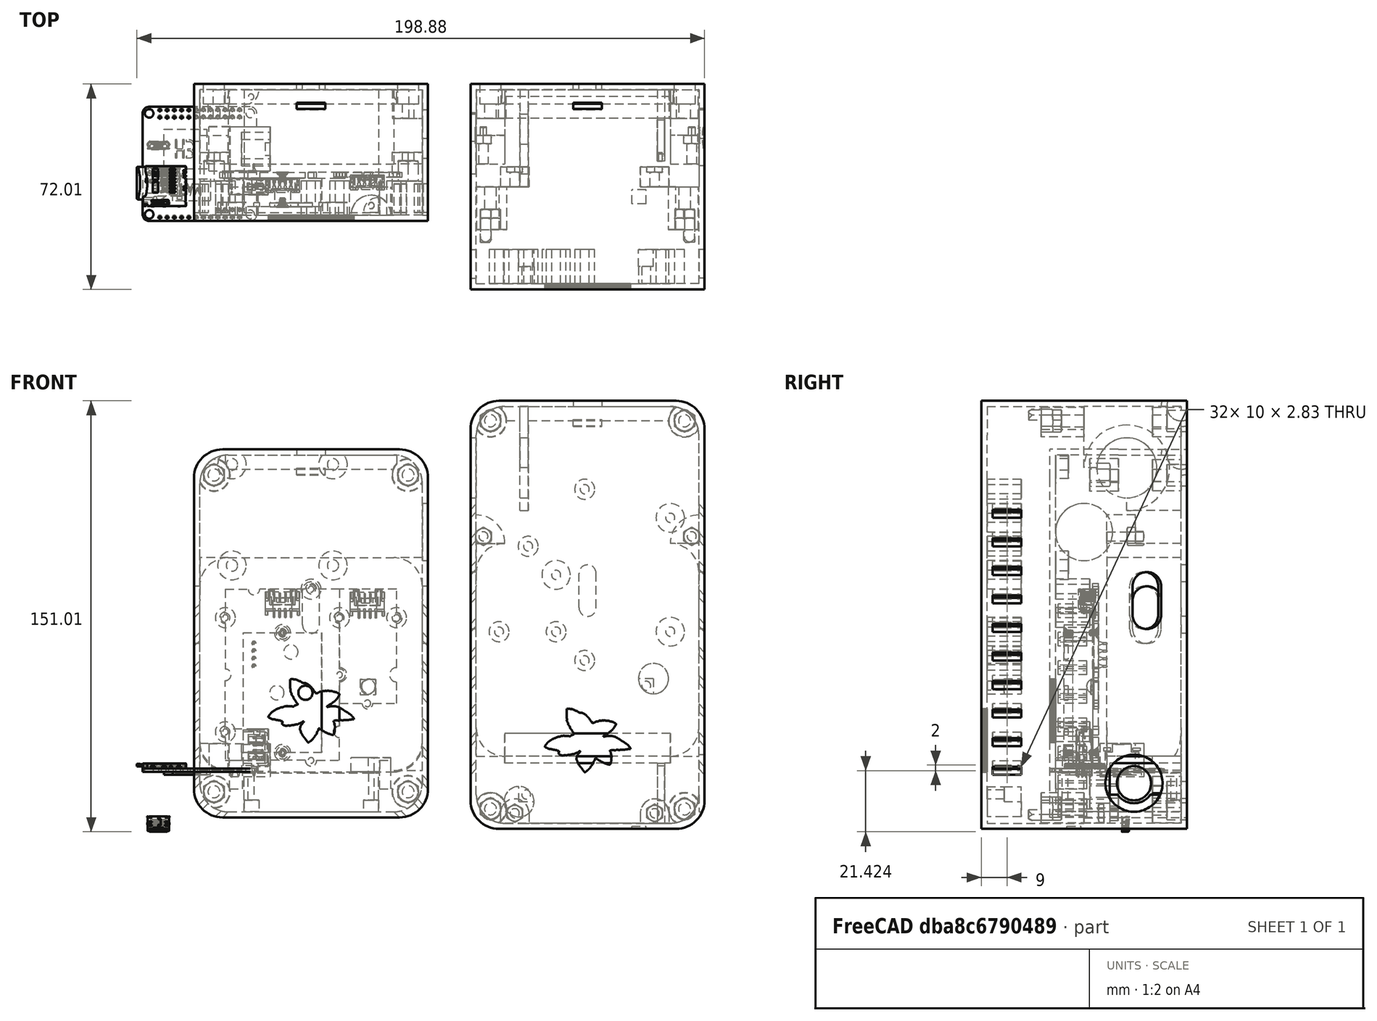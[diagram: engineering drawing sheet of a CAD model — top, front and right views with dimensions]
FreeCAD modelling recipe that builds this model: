
FCSTD DOCUMENT  (FreeCAD 0.20R29410 (Git))
Label: smallerFormFactor
License: All rights reserved
LicenseURL: http://en.wikipedia.org/wiki/All_rights_reserved
objects: Part::Cylinder×180, Part::Cut×129, Part::Box×128, Part::MultiFuse×102, Part::Feature×61, Mesh::Feature×3, App::Part×2, Part::FeaturePython×2
note: 602 computed .brp shape members not serialized (recipe doc carries the construction recipe); baked Part::Feature solids carry a one-line shape summary decoded from their .brp

FEATURE [Part::Feature] Part__Feature  label="NanoPi2_Board"
  shape: bbox 40 x 40 x 1.15 mm, 138 faces (baked)
FEATURE [Part::Feature] Part__Feature001  label="USB_stehend"
  Placement = pos=(16.95,-5.15,8.45) rot=(0.707107,0,0.707107;3.14159rad)
  shape: bbox 13.8 x 6.121 x 16.97 mm, 181 faces (baked)
FEATURE [Part::Feature] Part__Feature002  label="microUSB_Geh㴳e"
  Placement = pos=(-14.4796,6.47188,-20.7085) rot=(0,0,1;0rad)
  shape: bbox 6.984 x 2.203 x 4.218 mm, 441 faces (baked)
FEATURE [Part::Feature] Part__Feature003  label="micro_USB_Innenteil"
  Placement = pos=(-14.4796,6.47188,-16.0085) rot=(0,0,1;0rad)
  shape: bbox 8.008 x 2.958 x 5.47 mm, 792 faces (baked)
FEATURE [App::Part] microUSB
  Group = -> [Part__Feature002,Part__Feature003]
  Origin = -> Origin
  Placement = pos=(-36.1085,-4.22965,-4.14688) rot=(-0.57735,0.57735,0.57735;4.18879rad)
FEATURE [Part::Feature] Part__Feature004  label="microSD Card Connector"
  Placement = pos=(-12.36,-7.8,1.95) rot=(0,0,-1;1.5708rad)
  shape: bbox 15.2 x 14.1 x 1.892 mm, 638 faces (baked)
FEATURE [Part::Feature] Part__Feature005  label="RJ45_tief"
  Placement = pos=(24.7,5.25,4.15) rot=(0,0,1;1.5708rad)
  shape: bbox 21.5 x 15.5 x 11.5 mm, 30 faces (baked)
FEATURE [Part::Feature] Part__Feature006  label="microSD_Card"
  Placement = pos=(-6.76,-12.42,1.9) rot=(1,0,0;1.5708rad)
  shape: bbox 15.24 x 11.43 x 0.889 mm, 332 faces (baked)
FEATURE [Part::Feature] Part__Feature007  label="RAM"
  Placement = pos=(-2.9,-9.1,0) rot=(1,0,0;3.14159rad)
  shape: bbox 13.21 x 7.809 x 1.009 mm, 46 faces (baked)
FEATURE [Part::Feature] Part__Feature008  label="Prozessor_H3"
  Placement = pos=(-5,5.2,1e-15) rot=(1,0,0;3.14159rad)
  shape: bbox 15.01 x 14.01 x 1.009 mm, 28 faces (baked)
FEATURE [Part::Feature] Feature001  label="SCD30"
  Placement = pos=(9,-5,64) rot=(0,1,0;1.5708rad)
  shape: bbox 44 x 15.1 x 64 mm, 422 faces, 13 solids (baked)
FEATURE [Part::Feature] Feature002  label="bme280"
  Placement = pos=(69,-3,63) rot=(0.707107,0,-0.707107;3.14159rad)
  shape: bbox 23.8 x 6.016 x 41.9 mm, 221 faces, 2 solids (baked)
FEATURE [Part::Box] Box001  label="ips7100"
  AttacherType = Attacher::AttachEngine3D
  Height = 43.1
  Length = 47.1
  Width = 13.55
FEATURE [Part::Cylinder] Cylinder
  Angle = 360
  AttacherType = Attacher::AttachEngine3D
  FirstAngle = 0
  Height = 13.55
  Placement = pos=(2.5,13.55,2.5) rot=(1,0,0;1.5708rad)
  Radius = 1
  SecondAngle = 0
FEATURE [Part::Cylinder] Cylinder001  label="semiCut"
  Angle = 90
  AttacherType = Attacher::AttachEngine3D
  FirstAngle = 0
  Height = 4.13
  Placement = pos=(0,4.13,-9e-16) rot=(1,0,0;1.5708rad)
  Radius = 5.25
  SecondAngle = 0
FEATURE [Part::Cylinder] Cylinder002
  Angle = 360
  AttacherType = Attacher::AttachEngine3D
  FirstAngle = 0
  Height = 13.55
  Placement = pos=(2.5,13.55,2.5) rot=(1,0,0;1.5708rad)
  Radius = 1
  SecondAngle = 0
FEATURE [Part::Cylinder] Cylinder003  label="semiCut001"
  Angle = 90
  AttacherType = Attacher::AttachEngine3D
  FirstAngle = 0
  Height = 4.13
  Placement = pos=(0,4.13,-9e-16) rot=(1,0,0;1.5708rad)
  Radius = 5.25
  SecondAngle = 0
FEATURE [Part::MultiFuse] Fusion001  label="ipsCut"
  Shapes = -> [Cylinder,Cylinder001]
FEATURE [Part::MultiFuse] Fusion002  label="ipsCut001"
  Placement = pos=(47.1,0,43.1) rot=(0,1,0;3.14159rad)
  Shapes = -> [Cylinder002,Cylinder003]
FEATURE [Part::MultiFuse] Fusion003
  Shapes = -> [Fusion001,Fusion002]
FEATURE [Part::Cut] Cut  label="ips7100V"
  Base = -> Box001
  Placement = pos=(15.5,26,-14) rot=(1,0,0;1.5708rad)
  Tool = -> Fusion003
FEATURE [Part::Box] Box002  label="V25B"
  AttacherType = Attacher::AttachEngine3D
  Height = 75
  Length = 78
  Width = 26
FEATURE [Part::Box] Box003  label="Cube001"
  AttacherType = Attacher::AttachEngine3D
  Height = 10
  Length = 10
  Width = 26
FEATURE [Part::Box] Box004  label="Cube002"
  AttacherType = Attacher::AttachEngine3D
  Height = 10
  Length = 10
  Width = 26
FEATURE [Part::Box] Box005  label="Cube003"
  AttacherType = Attacher::AttachEngine3D
  Height = 10
  Length = 10
  Width = 26
FEATURE [Part::Box] Box006  label="Cube004"
  AttacherType = Attacher::AttachEngine3D
  Height = 10
  Length = 10
  Width = 26
FEATURE [Part::Cylinder] Cylinder004
  Angle = 90
  AttacherType = Attacher::AttachEngine3D
  FirstAngle = 0
  Height = 26
  Placement = pos=(0,26,-5.8e-15) rot=(1,0,0;1.5708rad)
  Radius = 10
  SecondAngle = 0
FEATURE [Part::Cut] Cut001
  Base = -> Box003
  Placement = pos=(68,0,65) rot=(0,0,1;0rad)
  Tool = -> Cylinder004
FEATURE [Part::Cylinder] Cylinder005
  Angle = 90
  AttacherType = Attacher::AttachEngine3D
  FirstAngle = 0
  Height = 26
  Placement = pos=(0,26,-5.8e-15) rot=(1,0,0;1.5708rad)
  Radius = 10
  SecondAngle = 0
FEATURE [Part::Cut] Cut002
  Base = -> Box004
  Placement = pos=(68,0,10) rot=(0,1,0;1.5708rad)
  Tool = -> Cylinder005
FEATURE [Part::Cylinder] Cylinder006
  Angle = 90
  AttacherType = Attacher::AttachEngine3D
  FirstAngle = 0
  Height = 26
  Placement = pos=(0,26,-5.8e-15) rot=(1,0,0;1.5708rad)
  Radius = 10
  SecondAngle = 0
FEATURE [Part::Cut] Cut003
  Base = -> Box005
  Placement = pos=(10,0,10) rot=(0,1,0;3.14159rad)
  Tool = -> Cylinder006
FEATURE [Part::Cylinder] Cylinder007
  Angle = 90
  AttacherType = Attacher::AttachEngine3D
  FirstAngle = 0
  Height = 26
  Placement = pos=(0,26,-5.8e-15) rot=(1,0,0;1.5708rad)
  Radius = 10
  SecondAngle = 0
FEATURE [Part::Cut] Cut004
  Base = -> Box006
  Placement = pos=(10,0,65) rot=(0,-1,0;1.5708rad)
  Tool = -> Cylinder007
FEATURE [Part::MultiFuse] Fusion004  label="v25Cuts"
  Shapes = -> [Cut001,Cut002,Cut003,Cut004]
FEATURE [Part::Cut] Cut005  label="V25B001"
  Base = -> Box002
  Tool = -> Fusion004
FEATURE [Part::Box] Box009  label="Cube007"
  AttacherType = Attacher::AttachEngine3D
  Height = 10
  Length = 10
  Placement = pos=(0,-10,0) rot=(0,0,1;0rad)
  Width = 36
FEATURE [Part::Box] Box010  label="baseOut001"
  AttacherType = Attacher::AttachEngine3D
  Height = 150
  Length = 82
  Placement = pos=(80,26,-2) rot=(0,0,1;3.14159rad)
  Width = 36
FEATURE [Part::Box] Box011  label="Cube008"
  AttacherType = Attacher::AttachEngine3D
  Height = 10
  Length = 10
  Placement = pos=(0,-10,0) rot=(0,0,1;0rad)
  Width = 36
FEATURE [Part::Box] Box012  label="Cube009"
  AttacherType = Attacher::AttachEngine3D
  Height = 10
  Length = 10
  Placement = pos=(0,-10,0) rot=(0,0,1;0rad)
  Width = 36
FEATURE [Part::Box] Box013  label="Cube010"
  AttacherType = Attacher::AttachEngine3D
  Height = 10
  Length = 10
  Placement = pos=(0,-10,0) rot=(0,0,1;0rad)
  Width = 36
FEATURE [Part::Box] Box014  label="Cube011"
  AttacherType = Attacher::AttachEngine3D
  Height = 10
  Length = 10
  Placement = pos=(0,-8,0) rot=(0,0,1;0rad)
  Width = 34
FEATURE [Part::Box] Box015  label="baseOut002"
  AttacherType = Attacher::AttachEngine3D
  Height = 146
  Length = 78
  Placement = pos=(80,26,-2) rot=(0,0,1;3.14159rad)
  Width = 34
FEATURE [Part::Box] Box016  label="Cube012"
  AttacherType = Attacher::AttachEngine3D
  Height = 10
  Length = 10
  Placement = pos=(0,-8,0) rot=(0,0,1;0rad)
  Width = 34
FEATURE [Part::Box] Box017  label="Cube013"
  AttacherType = Attacher::AttachEngine3D
  Height = 10
  Length = 10
  Placement = pos=(0,-8,0) rot=(0,0,1;0rad)
  Width = 34
FEATURE [Part::Box] Box018  label="Cube014"
  AttacherType = Attacher::AttachEngine3D
  Height = 10
  Length = 10
  Placement = pos=(0,-8,0) rot=(0,0,1;0rad)
  Width = 34
FEATURE [Part::Box] Box019  label="Cube015"
  AttacherType = Attacher::AttachEngine3D
  Height = 10
  Length = 10
  Placement = pos=(10,26,0) rot=(0,0,1;3.14159rad)
  Width = 26
FEATURE [Part::Box] Box020  label="Cube016"
  AttacherType = Attacher::AttachEngine3D
  Height = 10
  Length = 10
  Placement = pos=(10,26,0) rot=(0,0,1;3.14159rad)
  Width = 26
FEATURE [Part::Box] Box021  label="Cube017"
  AttacherType = Attacher::AttachEngine3D
  Height = 10
  Length = 10
  Placement = pos=(10,26,0) rot=(0,0,1;3.14159rad)
  Width = 26
FEATURE [Part::Box] Box022  label="Cube018"
  AttacherType = Attacher::AttachEngine3D
  Height = 10
  Length = 10
  Placement = pos=(10,26,0) rot=(0,0,1;3.14159rad)
  Width = 26
FEATURE [Part::Box] Box023  label="Cube019"
  AttacherType = Attacher::AttachEngine3D
  Height = 4
  Length = 10
  Placement = pos=(8.5,-3,4) rot=(1,0,0;3.14159rad)
  Width = 7
FEATURE [Part::Box] Box024  label="Cube020"
  AttacherType = Attacher::AttachEngine3D
  Height = 4
  Length = 10
  Placement = pos=(57.5,-3,4) rot=(1,0,0;3.14159rad)
  Width = 7
FEATURE [Part::Box] Box025  label="Cube021"
  AttacherType = Attacher::AttachEngine3D
  Height = 22
  Length = 2.5
  Placement = pos=(63.5,24,21) rot=(1,0,0;3.14159rad)
  Width = 25
FEATURE [Part::Box] Box028  label="Cube023"
  AttacherType = Attacher::AttachEngine3D
  Height = 10
  Length = 10
  Placement = pos=(0,-10,0) rot=(0,0,1;0rad)
  Width = 36
FEATURE [Part::Box] Box029  label="baseOut003"
  AttacherType = Attacher::AttachEngine3D
  Height = 150
  Length = 82
  Placement = pos=(80,26,-2) rot=(0,0,1;3.14159rad)
  Width = 36
FEATURE [Part::Box] Box030  label="Cube024"
  AttacherType = Attacher::AttachEngine3D
  Height = 10
  Length = 10
  Placement = pos=(0,-10,0) rot=(0,0,1;0rad)
  Width = 36
FEATURE [Part::Box] Box031  label="Cube025"
  AttacherType = Attacher::AttachEngine3D
  Height = 10
  Length = 10
  Placement = pos=(0,-10,0) rot=(0,0,1;0rad)
  Width = 36
FEATURE [Part::Box] Box032  label="Cube026"
  AttacherType = Attacher::AttachEngine3D
  Height = 10
  Length = 10
  Placement = pos=(0,-10,0) rot=(0,0,1;0rad)
  Width = 36
FEATURE [Part::Box] Box033  label="Cube027"
  AttacherType = Attacher::AttachEngine3D
  Height = 10
  Length = 10
  Placement = pos=(0,-8,0) rot=(0,0,1;0rad)
  Width = 34
FEATURE [Part::Box] Box034  label="baseOut004"
  AttacherType = Attacher::AttachEngine3D
  Height = 146
  Length = 78
  Placement = pos=(80,26,-2) rot=(0,0,1;3.14159rad)
  Width = 34
FEATURE [Part::Box] Box035  label="Cube028"
  AttacherType = Attacher::AttachEngine3D
  Height = 10
  Length = 10
  Placement = pos=(0,-8,0) rot=(0,0,1;0rad)
  Width = 34
FEATURE [Part::Box] Box036  label="Cube029"
  AttacherType = Attacher::AttachEngine3D
  Height = 10
  Length = 10
  Placement = pos=(0,-8,0) rot=(0,0,1;0rad)
  Width = 34
FEATURE [Part::Box] Box037  label="Cube030"
  AttacherType = Attacher::AttachEngine3D
  Height = 10
  Length = 10
  Placement = pos=(0,-8,0) rot=(0,0,1;0rad)
  Width = 34
FEATURE [Part::Box] Box038  label="ethernetHold"
  AttacherType = Attacher::AttachEngine3D
  Height = 34
  Length = 3
  Placement = pos=(15.3,24,109.5) rot=(1,0,0;1.5708rad)
  Width = 37
FEATURE [Part::Box] Box042  label="Cube034"
  AttacherType = Attacher::AttachEngine3D
  Height = 12
  Length = 6
  Placement = pos=(3,0,44) rot=(0,0,1;0rad)
  Width = 2
FEATURE [Part::Box] Box043  label="lightCut"
  AttacherType = Attacher::AttachEngine3D
  Height = 5
  Length = 5
  Placement = pos=(54.5,-16,-6) rot=(0,0,1;0rad)
  Width = 5
FEATURE [Part::Box] Box045  label="Cube036"
  AttacherType = Attacher::AttachEngine3D
  Height = 2
  Length = 20
  Placement = pos=(0,0,0) rot=(0,-1,0;0.785398rad)
  Width = 10
FEATURE [Part::Box] Box046  label="Cube037"
  AttacherType = Attacher::AttachEngine3D
  Height = 2
  Length = 20
  Placement = pos=(0,0,10) rot=(0,-1,0;0.785398rad)
  Width = 10
FEATURE [Part::Box] Box047  label="Cube038"
  AttacherType = Attacher::AttachEngine3D
  Height = 2
  Length = 20
  Placement = pos=(0,0,20) rot=(0,-1,0;0.785398rad)
  Width = 10
FEATURE [Part::Box] Box048  label="Cube039"
  AttacherType = Attacher::AttachEngine3D
  Height = 2
  Length = 20
  Placement = pos=(0,0,30) rot=(0,-1,0;0.785398rad)
  Width = 10
FEATURE [Part::Box] Box049  label="Cube040"
  AttacherType = Attacher::AttachEngine3D
  Height = 2
  Length = 10
  Placement = pos=(0,0,40) rot=(0,-1,0;0.785398rad)
  Width = 10
FEATURE [Part::Box] Box050  label="Cube041"
  AttacherType = Attacher::AttachEngine3D
  Height = 2
  Length = 20
  Placement = pos=(0,0,50) rot=(0,-1,0;0.785398rad)
  Width = 10
FEATURE [Part::Box] Box051  label="Cube042"
  AttacherType = Attacher::AttachEngine3D
  Height = 2
  Length = 20
  Placement = pos=(0,0,60) rot=(0,-1,0;0.785398rad)
  Width = 10
FEATURE [Part::Box] Box052  label="Cube043"
  AttacherType = Attacher::AttachEngine3D
  Height = 2
  Length = 20
  Placement = pos=(0,0,70) rot=(0,-1,0;0.785398rad)
  Width = 10
FEATURE [Part::Box] Box053  label="Cube044"
  AttacherType = Attacher::AttachEngine3D
  Height = 2
  Length = 20
  Placement = pos=(0,0,80) rot=(0,-1,0;0.785398rad)
  Width = 10
FEATURE [Part::Box] Box054  label="Cube045"
  AttacherType = Attacher::AttachEngine3D
  Height = 2
  Length = 20
  Placement = pos=(0,0,90) rot=(0,-1,0;0.785398rad)
  Width = 10
FEATURE [Part::Box] Box055  label="Cube046"
  AttacherType = Attacher::AttachEngine3D
  Height = 2
  Length = 20
  Placement = pos=(0,0,1000) rot=(0,-1,0;0.785398rad)
  Width = 10
FEATURE [Part::Box] Box056  label="Cube047"
  AttacherType = Attacher::AttachEngine3D
  Height = 2
  Length = 20
  Placement = pos=(0,0,0) rot=(0,-1,0;0.785398rad)
  Width = 10
FEATURE [Part::Box] Box057  label="Cube048"
  AttacherType = Attacher::AttachEngine3D
  Height = 2
  Length = 20
  Placement = pos=(0,0,10) rot=(0,-1,0;0.785398rad)
  Width = 10
FEATURE [Part::Box] Box058  label="Cube049"
  AttacherType = Attacher::AttachEngine3D
  Height = 2
  Length = 20
  Placement = pos=(0,0,20) rot=(0,-1,0;0.785398rad)
  Width = 10
FEATURE [Part::Box] Box059  label="Cube050"
  AttacherType = Attacher::AttachEngine3D
  Height = 2
  Length = 20
  Placement = pos=(0,0,30) rot=(0,-1,0;0.785398rad)
  Width = 10
FEATURE [Part::Box] Box060  label="Cube051"
  AttacherType = Attacher::AttachEngine3D
  Height = 2
  Length = 10
  Placement = pos=(0,0,40) rot=(0,-1,0;0.785398rad)
  Width = 10
FEATURE [Part::Box] Box061  label="Cube052"
  AttacherType = Attacher::AttachEngine3D
  Height = 2
  Length = 20
  Placement = pos=(0,0,50) rot=(0,-1,0;0.785398rad)
  Width = 10
FEATURE [Part::Box] Box062  label="Cube053"
  AttacherType = Attacher::AttachEngine3D
  Height = 2
  Length = 20
  Placement = pos=(0,0,60) rot=(0,-1,0;0.785398rad)
  Width = 10
FEATURE [Part::Box] Box063  label="Cube054"
  AttacherType = Attacher::AttachEngine3D
  Height = 2
  Length = 20
  Placement = pos=(0,0,70) rot=(0,-1,0;0.785398rad)
  Width = 10
FEATURE [Part::Box] Box064  label="Cube055"
  AttacherType = Attacher::AttachEngine3D
  Height = 2
  Length = 10
  Placement = pos=(0,0,80) rot=(0,-1,0;0.785398rad)
  Width = 10
FEATURE [Part::Box] Box065  label="Cube056"
  AttacherType = Attacher::AttachEngine3D
  Height = 2
  Length = 20
  Placement = pos=(0,0,90) rot=(0,-1,0;0.785398rad)
  Width = 10
FEATURE [Part::Box] Box066  label="Cube057"
  AttacherType = Attacher::AttachEngine3D
  Height = 2
  Length = 20
  Placement = pos=(0,0,1000) rot=(0,-1,0;0.785398rad)
  Width = 10
FEATURE [Part::Box] Box070  label="Cube059"
  AttacherType = Attacher::AttachEngine3D
  Height = 2.5
  Length = 58
  Placement = pos=(68,24,21) rot=(0,0,1;3.14159rad)
  Width = 10
FEATURE [Part::Box] Box071  label="Cube060"
  AttacherType = Attacher::AttachEngine3D
  Height = 10.5
  Length = 58
  Placement = pos=(68,24,21) rot=(0,0,1;3.14159rad)
  Width = 10
FEATURE [Part::Box] Box072  label="Cube061"
  AttacherType = Attacher::AttachEngine3D
  Height = 1.5
  Length = 36
  Width = 29
FEATURE [Part::Box] Box073  label="Cube062"
  AttacherType = Attacher::AttachEngine3D
  Height = 5.5
  Length = 36
  Placement = pos=(0,0,3.6) rot=(0,0,1;0rad)
  Width = 29
FEATURE [Part::Box] Box074  label="usbCut002"
  AttacherType = Attacher::AttachEngine3D
  Height = 10
  Length = 82
  Width = 20
FEATURE [Part::Box] Box075  label="Cube063"
  AttacherType = Attacher::AttachEngine3D
  Height = 10
  Length = 82
  Width = 5
FEATURE [Part::Box] Box076  label="Cube064"
  AttacherType = Attacher::AttachEngine3D
  Height = 10
  Length = 82
  Width = 5
FEATURE [Part::Box] Box077  label="usbCut004"
  AttacherType = Attacher::AttachEngine3D
  Height = 10
  Length = 82
  Width = 20
FEATURE [Part::Box] Box078  label="Cube065"
  AttacherType = Attacher::AttachEngine3D
  Height = 10
  Length = 82
  Width = 5
FEATURE [Part::Box] Box079  label="Cube066"
  AttacherType = Attacher::AttachEngine3D
  Height = 10
  Length = 82
  Width = 5
FEATURE [Part::Box] Box080  label="ethernetHold001"
  AttacherType = Attacher::AttachEngine3D
  Height = 34
  Length = 3
  Placement = pos=(15.3,5,87.5) rot=(1,0,0;1.5708rad)
  Width = 37
FEATURE [Part::Feature] Clone001  label="m4Nut002"
  Placement = pos=(5,-22.5,141) rot=(-1,0,0;1.5708rad)
  shape: bbox 8.083 x 8.8 x 9.333 mm, 26 faces (baked)
FEATURE [Part::Feature] Clone002  label="m4Nut003"
  Placement = pos=(5,-22.5,141) rot=(-1,0,0;1.5708rad)
  shape: bbox 8.083 x 8.8 x 9.333 mm, 26 faces (baked)
FEATURE [Part::Feature] Clone003  label="m4Nut005"
  Placement = pos=(5,-22.5,141) rot=(-1,0,0;1.5708rad)
  shape: bbox 8.083 x 8.8 x 9.333 mm, 26 faces (baked)
FEATURE [Part::Feature] Clone004  label="m4Nut007"
  Placement = pos=(5,-22.5,141) rot=(-1,0,0;1.5708rad)
  shape: bbox 8.083 x 8.8 x 9.333 mm, 26 faces (baked)
FEATURE [Part::Feature] Clone006  label="m4Nut012"
  Placement = pos=(5,-22.5,141) rot=(-1,0,0;1.5708rad)
  shape: bbox 8.083 x 8.8 x 9.333 mm, 26 faces (baked)
FEATURE [Part::Feature] Clone007  label="m4Nut013"
  Placement = pos=(5,-22.5,141) rot=(-1,0,0;1.5708rad)
  shape: bbox 8.083 x 8.8 x 9.333 mm, 26 faces (baked)
FEATURE [Part::Feature] Clone008  label="m4Nut015"
  Placement = pos=(5,-22.5,141) rot=(-1,0,0;1.5708rad)
  shape: bbox 8.083 x 8.8 x 9.333 mm, 26 faces (baked)
FEATURE [Part::Feature] Clone009  label="m4Nut016"
  Placement = pos=(5,-22.5,141) rot=(-1,0,0;1.5708rad)
  shape: bbox 8.083 x 8.8 x 9.333 mm, 26 faces (baked)
FEATURE [Part::Cylinder] Cylinder008
  Angle = 90
  AttacherType = Attacher::AttachEngine3D
  FirstAngle = 0
  Height = 36
  Placement = pos=(0,26,-5.8e-15) rot=(1,0,0;1.5708rad)
  Radius = 10
  SecondAngle = 0
FEATURE [Part::Cut] Cut006
  Base = -> Box009
  Placement = pos=(8,18,8) rot=(0.707107,0,-0.707107;3.14159rad)
  Tool = -> Cylinder008
FEATURE [Part::Cylinder] Cylinder009
  Angle = 90
  AttacherType = Attacher::AttachEngine3D
  FirstAngle = 0
  Height = 36
  Placement = pos=(0,26,-5.8e-15) rot=(1,0,0;1.5708rad)
  Radius = 10
  SecondAngle = 0
FEATURE [Part::Cut] Cut007
  Base = -> Box011
  Placement = pos=(70,18,8) rot=(1,0,0;3.14159rad)
  Tool = -> Cylinder009
FEATURE [Part::Cylinder] Cylinder010
  Angle = 90
  AttacherType = Attacher::AttachEngine3D
  FirstAngle = 0
  Height = 36
  Placement = pos=(0,26,-5.8e-15) rot=(1,0,0;1.5708rad)
  Radius = 10
  SecondAngle = 0
FEATURE [Part::Cut] Cut008
  Base = -> Box012
  Placement = pos=(8,18,138) rot=(0,0,1;3.14159rad)
  Tool = -> Cylinder010
FEATURE [Part::Cylinder] Cylinder011
  Angle = 90
  AttacherType = Attacher::AttachEngine3D
  FirstAngle = 0
  Height = 36
  Placement = pos=(0,26,-5.8e-15) rot=(1,0,0;1.5708rad)
  Radius = 10
  SecondAngle = 0
FEATURE [Part::Cut] Cut009
  Base = -> Box013
  Placement = pos=(70,18,138) rot=(0.707107,0,0.707107;3.14159rad)
  Tool = -> Cylinder011
FEATURE [Part::Cylinder] Cylinder013
  Angle = 90
  AttacherType = Attacher::AttachEngine3D
  FirstAngle = 0
  Height = 34
  Placement = pos=(0,26,-5.8e-15) rot=(1,0,0;1.5708rad)
  Radius = 10
  SecondAngle = 0
FEATURE [Part::Cut] Cut012
  Base = -> Box014
  Placement = pos=(12,18,8) rot=(0.707107,0,-0.707107;3.14159rad)
  Tool = -> Cylinder013
FEATURE [Part::Cylinder] Cylinder014
  Angle = 90
  AttacherType = Attacher::AttachEngine3D
  FirstAngle = 0
  Height = 34
  Placement = pos=(0,26,-5.8e-15) rot=(1,0,0;1.5708rad)
  Radius = 10
  SecondAngle = 0
FEATURE [Part::Cut] Cut013
  Base = -> Box016
  Placement = pos=(70,18,8) rot=(1,0,0;3.14159rad)
  Tool = -> Cylinder014
FEATURE [Part::Cylinder] Cylinder015
  Angle = 90
  AttacherType = Attacher::AttachEngine3D
  FirstAngle = 0
  Height = 34
  Placement = pos=(0,26,-5.8e-15) rot=(1,0,0;1.5708rad)
  Radius = 10
  SecondAngle = 0
FEATURE [Part::Cut] Cut014
  Base = -> Box017
  Placement = pos=(12,18,134) rot=(0,0,1;3.14159rad)
  Tool = -> Cylinder015
FEATURE [Part::Cylinder] Cylinder016
  Angle = 90
  AttacherType = Attacher::AttachEngine3D
  FirstAngle = 0
  Height = 34
  Placement = pos=(0,26,-5.8e-15) rot=(1,0,0;1.5708rad)
  Radius = 10
  SecondAngle = 0
FEATURE [Part::Cut] Cut015
  Base = -> Box018
  Placement = pos=(70,18,134) rot=(0.707107,0,0.707107;3.14159rad)
  Tool = -> Cylinder016
FEATURE [Part::Cylinder] Cylinder017
  Angle = 90
  AttacherType = Attacher::AttachEngine3D
  FirstAngle = 0
  Height = 26
  Placement = pos=(0,26,-5.8e-15) rot=(1,0,0;1.5708rad)
  Radius = 10
  SecondAngle = 0
FEATURE [Part::Cut] Cut018  label="batterySupport"
  Base = -> Box019
  Placement = pos=(10,-2,33.5) rot=(0,1,0;3.14159rad)
  Tool = -> Cylinder017
FEATURE [Part::Cylinder] Cylinder018
  Angle = 90
  AttacherType = Attacher::AttachEngine3D
  FirstAngle = 0
  Height = 26
  Placement = pos=(0,26,-5.8e-15) rot=(1,0,0;1.5708rad)
  Radius = 10
  SecondAngle = 0
FEATURE [Part::Cut] Cut019  label="batterySupport001"
  Base = -> Box020
  Placement = pos=(68,-2,33.5) rot=(0,1,0;1.5708rad)
  Tool = -> Cylinder018
FEATURE [Part::Cylinder] Cylinder019
  Angle = 90
  AttacherType = Attacher::AttachEngine3D
  FirstAngle = 0
  Height = 26
  Placement = pos=(0,26,-5.8e-15) rot=(1,0,0;1.5708rad)
  Radius = 10
  SecondAngle = 0
FEATURE [Part::Cut] Cut020  label="batterySupport002"
  Base = -> Box021
  Placement = pos=(68,-2,88) rot=(0,0,1;0rad)
  Tool = -> Cylinder019
FEATURE [Part::Cylinder] Cylinder020
  Angle = 90
  AttacherType = Attacher::AttachEngine3D
  FirstAngle = 0
  Height = 26
  Placement = pos=(0,26,-5.8e-15) rot=(1,0,0;1.5708rad)
  Radius = 10
  SecondAngle = 0
FEATURE [Part::Cut] Cut021  label="batterySupport003"
  Base = -> Box022
  Placement = pos=(10,-2,88) rot=(0,-1,0;1.5708rad)
  Tool = -> Cylinder020
FEATURE [Part::Cylinder] Cylinder021
  Angle = 360
  AttacherType = Attacher::AttachEngine3D
  FirstAngle = 0
  Height = 7
  Placement = pos=(13.5,-3,3.5) rot=(1,0,0;1.5708rad)
  Radius = 5
  SecondAngle = 0
FEATURE [Part::Cylinder] Cylinder022
  Angle = 360
  AttacherType = Attacher::AttachEngine3D
  FirstAngle = 0
  Height = 8
  Placement = pos=(13.5,-2,3.5) rot=(1,0,0;1.5708rad)
  Radius = 1.6
  SecondAngle = 0
FEATURE [Part::Cylinder] Cylinder023
  Angle = 360
  AttacherType = Attacher::AttachEngine3D
  FirstAngle = 0
  Height = 7
  Placement = pos=(62.5,-3,3.5) rot=(1,0,0;1.5708rad)
  Radius = 5
  SecondAngle = 0
FEATURE [Part::Cylinder] Cylinder024
  Angle = 360
  AttacherType = Attacher::AttachEngine3D
  FirstAngle = 0
  Height = 8
  Placement = pos=(62.5,-2,3.5) rot=(1,0,0;1.5708rad)
  Radius = 1.6
  SecondAngle = 0
FEATURE [Part::Cylinder] Cylinder025
  Angle = 360
  AttacherType = Attacher::AttachEngine3D
  FirstAngle = 0
  Height = 20
  Radius = 6
  SecondAngle = 0
FEATURE [Part::Cylinder] Cylinder026
  Angle = 360
  AttacherType = Attacher::AttachEngine3D
  FirstAngle = 0
  Height = 5
  Radius = 7
  SecondAngle = 0
FEATURE [Part::Cylinder] Cylinder027  label="mainMounts"
  Angle = 90
  AttacherType = Attacher::AttachEngine3D
  FirstAngle = 0
  Height = 10
  Placement = pos=(0,24,98) rot=(1,0,0;1.5708rad)
  Radius = 10
  SecondAngle = 0
FEATURE [Part::Cylinder] Cylinder028  label="mainMounts001"
  Angle = 90
  AttacherType = Attacher::AttachEngine3D
  FirstAngle = 0
  Height = 10
  Placement = pos=(78,24,98) rot=(0.57735,-0.57735,0.57735;2.0944rad)
  Radius = 10
  SecondAngle = 0
FEATURE [Part::Cylinder] Cylinder029
  Angle = 360
  AttacherType = Attacher::AttachEngine3D
  FirstAngle = 0
  Height = 10
  Placement = pos=(2.5,-2,100.5) rot=(1,0,0;1.5708rad)
  Radius = 1.6
  SecondAngle = 0
FEATURE [Part::Cylinder] Cylinder030
  Angle = 360
  AttacherType = Attacher::AttachEngine3D
  FirstAngle = 0
  Height = 10
  Placement = pos=(75.5,-2,100.5) rot=(1,0,0;1.5708rad)
  Radius = 1.6
  SecondAngle = 0
FEATURE [Part::Cylinder] Cylinder040
  Angle = 90
  AttacherType = Attacher::AttachEngine3D
  FirstAngle = 0
  Height = 36
  Placement = pos=(0,26,-5.8e-15) rot=(1,0,0;1.5708rad)
  Radius = 10
  SecondAngle = 0
FEATURE [Part::Cut] Cut025
  Base = -> Box028
  Placement = pos=(8,18,8) rot=(0.707107,0,-0.707107;3.14159rad)
  Tool = -> Cylinder040
FEATURE [Part::Cylinder] Cylinder041
  Angle = 90
  AttacherType = Attacher::AttachEngine3D
  FirstAngle = 0
  Height = 36
  Placement = pos=(0,26,-5.8e-15) rot=(1,0,0;1.5708rad)
  Radius = 10
  SecondAngle = 0
FEATURE [Part::Cut] Cut026
  Base = -> Box030
  Placement = pos=(70,18,8) rot=(1,0,0;3.14159rad)
  Tool = -> Cylinder041
FEATURE [Part::Cylinder] Cylinder042
  Angle = 90
  AttacherType = Attacher::AttachEngine3D
  FirstAngle = 0
  Height = 36
  Placement = pos=(0,26,-5.8e-15) rot=(1,0,0;1.5708rad)
  Radius = 10
  SecondAngle = 0
FEATURE [Part::Cut] Cut027
  Base = -> Box031
  Placement = pos=(8,18,138) rot=(0,0,1;3.14159rad)
  Tool = -> Cylinder042
FEATURE [Part::Cylinder] Cylinder043
  Angle = 90
  AttacherType = Attacher::AttachEngine3D
  FirstAngle = 0
  Height = 36
  Placement = pos=(0,26,-5.8e-15) rot=(1,0,0;1.5708rad)
  Radius = 10
  SecondAngle = 0
FEATURE [Part::Cut] Cut028
  Base = -> Box032
  Placement = pos=(70,18,138) rot=(0.707107,0,0.707107;3.14159rad)
  Tool = -> Cylinder043
FEATURE [Part::Cylinder] Cylinder044
  Angle = 90
  AttacherType = Attacher::AttachEngine3D
  FirstAngle = 0
  Height = 34
  Placement = pos=(0,26,-5.8e-15) rot=(1,0,0;1.5708rad)
  Radius = 10
  SecondAngle = 0
FEATURE [Part::Cut] Cut030
  Base = -> Box033
  Placement = pos=(12,18,8) rot=(0.707107,0,-0.707107;3.14159rad)
  Tool = -> Cylinder044
FEATURE [Part::Cylinder] Cylinder045
  Angle = 90
  AttacherType = Attacher::AttachEngine3D
  FirstAngle = 0
  Height = 34
  Placement = pos=(0,26,-5.8e-15) rot=(1,0,0;1.5708rad)
  Radius = 10
  SecondAngle = 0
FEATURE [Part::Cut] Cut031
  Base = -> Box035
  Placement = pos=(70,18,8) rot=(1,0,0;3.14159rad)
  Tool = -> Cylinder045
FEATURE [Part::Cylinder] Cylinder046
  Angle = 90
  AttacherType = Attacher::AttachEngine3D
  FirstAngle = 0
  Height = 34
  Placement = pos=(0,26,-5.8e-15) rot=(1,0,0;1.5708rad)
  Radius = 10
  SecondAngle = 0
FEATURE [Part::Cut] Cut032
  Base = -> Box036
  Placement = pos=(12,18,134) rot=(0,0,1;3.14159rad)
  Tool = -> Cylinder046
FEATURE [Part::Cylinder] Cylinder047
  Angle = 90
  AttacherType = Attacher::AttachEngine3D
  FirstAngle = 0
  Height = 34
  Placement = pos=(0,26,-5.8e-15) rot=(1,0,0;1.5708rad)
  Radius = 10
  SecondAngle = 0
FEATURE [Part::Cut] Cut033
  Base = -> Box037
  Placement = pos=(70,18,134) rot=(0.707107,0,0.707107;3.14159rad)
  Tool = -> Cylinder047
FEATURE [Part::Cylinder] Cylinder048
  Angle = 360
  AttacherType = Attacher::AttachEngine3D
  FirstAngle = 0
  Height = 6
  Placement = pos=(17.5,-44,10.05) rot=(-1,0,0;1.5708rad)
  Radius = 1.57
  SecondAngle = 0
FEATURE [Part::Cylinder] Cylinder049
  Angle = 360
  AttacherType = Attacher::AttachEngine3D
  FirstAngle = 0
  Height = 6
  Placement = pos=(15,-44,7.55) rot=(0.57735,0.57735,0.57735;4.18879rad)
  Radius = 5.3
  SecondAngle = 0
FEATURE [Part::Cut] Cut036
  Base = -> Cylinder049
  Tool = -> Cylinder048
FEATURE [Part::Cylinder] Cylinder050
  Angle = 360
  AttacherType = Attacher::AttachEngine3D
  FirstAngle = 0
  Height = 6
  Placement = pos=(62.1,-44,50.65) rot=(0.57735,-0.57735,-0.57735;4.18879rad)
  Radius = 5.3
  SecondAngle = 0
FEATURE [Part::Cylinder] Cylinder051
  Angle = 360
  AttacherType = Attacher::AttachEngine3D
  FirstAngle = 0
  Height = 6
  Placement = pos=(59.6,-44,48.15) rot=(-1,0,0;1.5708rad)
  Radius = 1.57
  SecondAngle = 0
FEATURE [Part::Cut] Cut037
  Base = -> Cylinder050
  Tool = -> Cylinder051
FEATURE [Part::Cylinder] Cylinder052
  Angle = 270
  AttacherType = Attacher::AttachEngine3D
  FirstAngle = 0
  Height = 6
  Placement = pos=(15,-38,7.55) rot=(-1,0,0;1.5708rad)
  Radius = 5.3
  SecondAngle = 0
FEATURE [Part::Cylinder] Cylinder053
  Angle = 270
  AttacherType = Attacher::AttachEngine3D
  FirstAngle = 0
  Height = 6
  Placement = pos=(62.1,-38,50.65) rot=(0,0.707107,0.707107;3.14159rad)
  Radius = 5.3
  SecondAngle = 0
FEATURE [Part::Cylinder] Cylinder054  label="m2HeatSet001"
  Angle = 360
  AttacherType = Attacher::AttachEngine3D
  FirstAngle = 0
  Height = 12
  Placement = pos=(8,-44,67.1) rot=(-1,0,0;1.5708rad)
  Radius = 1.6
  SecondAngle = 0
FEATURE [Part::Cylinder] Cylinder055  label="m2HeatSet002"
  Angle = 360
  AttacherType = Attacher::AttachEngine3D
  FirstAngle = 0
  Height = 12
  Placement = pos=(28,-44,67.1) rot=(-1,0,0;1.5708rad)
  Radius = 1.6
  SecondAngle = 0
FEATURE [Part::Cylinder] Cylinder056  label="m2HeatSet003"
  Angle = 360
  AttacherType = Attacher::AttachEngine3D
  FirstAngle = 0
  Height = 12
  Placement = pos=(68,-44,67.1) rot=(-1,0,0;1.5708rad)
  Radius = 1.6
  SecondAngle = 0
FEATURE [Part::Cylinder] Cylinder057  label="m2HeatSet004"
  Angle = 360
  AttacherType = Attacher::AttachEngine3D
  FirstAngle = 0
  Height = 12
  Placement = pos=(18.2,-44,97) rot=(-1,0,0;1.5708rad)
  Radius = 1.6
  SecondAngle = 0
FEATURE [Part::Cylinder] Cylinder058  label="m2HeatSet005"
  Angle = 360
  AttacherType = Attacher::AttachEngine3D
  FirstAngle = 0
  Height = 12
  Placement = pos=(28,-44,87) rot=(-1,0,0;1.5708rad)
  Radius = 1.6
  SecondAngle = 0
FEATURE [Part::Cylinder] Cylinder059  label="m2HeatSet006"
  Angle = 360
  AttacherType = Attacher::AttachEngine3D
  FirstAngle = 0
  Height = 12
  Placement = pos=(38,-44,117) rot=(-1,0,0;1.5708rad)
  Radius = 1.6
  SecondAngle = 0
FEATURE [Part::Cylinder] Cylinder060  label="m2HeatSet007"
  Angle = 360
  AttacherType = Attacher::AttachEngine3D
  FirstAngle = 0
  Height = 12
  Placement = pos=(38,-44,57) rot=(-1,0,0;1.5708rad)
  Radius = 1.6
  SecondAngle = 0
FEATURE [Part::Cylinder] Cylinder061  label="m2HeatSet008"
  Angle = 360
  AttacherType = Attacher::AttachEngine3D
  FirstAngle = 0
  Height = 12
  Placement = pos=(68,-44,107) rot=(-1,0,0;1.5708rad)
  Radius = 1.6
  SecondAngle = 0
FEATURE [Part::Cylinder] Cylinder062  label="m2HeatSetOut"
  Angle = 360
  AttacherType = Attacher::AttachEngine3D
  FirstAngle = 0
  Height = 12
  Placement = pos=(8,-44,67.1) rot=(-1,0,0;1.5708rad)
  Radius = 3.5
  SecondAngle = 0
FEATURE [Part::Cylinder] Cylinder063  label="m2HeatSetOut001"
  Angle = 360
  AttacherType = Attacher::AttachEngine3D
  FirstAngle = 0
  Height = 12
  Placement = pos=(28,-44,67.1) rot=(-1,0,0;1.5708rad)
  Radius = 3.5
  SecondAngle = 0
FEATURE [Part::Cylinder] Cylinder064  label="m2HeatSetOut002"
  Angle = 360
  AttacherType = Attacher::AttachEngine3D
  FirstAngle = 0
  Height = 12
  Placement = pos=(18.2,-44,97) rot=(-1,0,0;1.5708rad)
  Radius = 3.5
  SecondAngle = 0
FEATURE [Part::Cylinder] Cylinder065  label="m2HeatSetOut003"
  Angle = 360
  AttacherType = Attacher::AttachEngine3D
  FirstAngle = 0
  Height = 12
  Placement = pos=(68,-44,67.1) rot=(-1,0,0;1.5708rad)
  Radius = 5
  SecondAngle = 0
FEATURE [Part::Cylinder] Cylinder066  label="m2HeatSetOut004"
  Angle = 360
  AttacherType = Attacher::AttachEngine3D
  FirstAngle = 0
  Height = 12
  Placement = pos=(28,-44,87) rot=(-1,0,0;1.5708rad)
  Radius = 5
  SecondAngle = 0
FEATURE [Part::Cylinder] Cylinder067  label="m2HeatSetOut005"
  Angle = 360
  AttacherType = Attacher::AttachEngine3D
  FirstAngle = 0
  Height = 12
  Placement = pos=(38,-44,57) rot=(-1,0,0;1.5708rad)
  Radius = 3.5
  SecondAngle = 0
FEATURE [Part::Cylinder] Cylinder068  label="m2HeatSetOut006"
  Angle = 360
  AttacherType = Attacher::AttachEngine3D
  FirstAngle = 0
  Height = 12
  Placement = pos=(68,-44,107) rot=(-1,0,0;1.5708rad)
  Radius = 5
  SecondAngle = 0
FEATURE [Part::Cylinder] Cylinder069  label="m2HeatSetOut007"
  Angle = 360
  AttacherType = Attacher::AttachEngine3D
  FirstAngle = 0
  Height = 12
  Placement = pos=(38,-44,117) rot=(-1,0,0;1.5708rad)
  Radius = 3.5
  SecondAngle = 0
FEATURE [Part::Cylinder] Cylinder073  label="m4SupportDisk"
  Angle = 360
  AttacherType = Attacher::AttachEngine3D
  FirstAngle = 0
  Height = 15
  Placement = pos=(5,-25,141) rot=(-1,0,0;1.5708rad)
  Radius = 5.69
  SecondAngle = 0
FEATURE [Part::Cylinder] Cylinder080  label="m2HeatSetOut008"
  Angle = 360
  AttacherType = Attacher::AttachEngine3D
  FirstAngle = 0
  Height = 12
  Placement = pos=(8,-44,67.1) rot=(-1,0,0;1.5708rad)
  Radius = 3.5
  SecondAngle = 0
FEATURE [Part::Cylinder] Cylinder081  label="m2HeatSet009"
  Angle = 360
  AttacherType = Attacher::AttachEngine3D
  FirstAngle = 0
  Height = 12
  Placement = pos=(8,-44,67.1) rot=(-1,0,0;1.5708rad)
  Radius = 1.6
  SecondAngle = 0
FEATURE [Part::Cut] Cut043  label="m2HeatSet010"
  Base = -> Cylinder080
  Tool = -> Cylinder081
FEATURE [Part::Cylinder] Cylinder084  label="m4HoleBase006"
  Angle = 360
  AttacherType = Attacher::AttachEngine3D
  FirstAngle = 0
  Height = 12
  Placement = pos=(73,26,5) rot=(0,0.707107,-0.707107;3.14159rad)
  Radius = 5.5
  SecondAngle = 0
FEATURE [Part::Cylinder] Cylinder085  label="m4HoleBaseCut"
  Angle = 360
  AttacherType = Attacher::AttachEngine3D
  FirstAngle = 0
  Height = 7
  Placement = pos=(73,26,5) rot=(0,0.707107,-0.707107;3.14159rad)
  Radius = 3.75
  SecondAngle = 0
FEATURE [Part::Cylinder] Cylinder086  label="m4HoleBase007"
  Angle = 360
  AttacherType = Attacher::AttachEngine3D
  FirstAngle = 0
  Height = 12
  Placement = pos=(5,26,5) rot=(0,0.707107,-0.707107;3.14159rad)
  Radius = 5.5
  SecondAngle = 0
FEATURE [Part::Cylinder] Cylinder087  label="m4HoleBaseCut001"
  Angle = 360
  AttacherType = Attacher::AttachEngine3D
  FirstAngle = 0
  Height = 7
  Placement = pos=(5,26,5) rot=(0,0.707107,-0.707107;3.14159rad)
  Radius = 3.75
  SecondAngle = 0
FEATURE [Part::Cylinder] Cylinder088  label="m4HoleBase008"
  Angle = 360
  AttacherType = Attacher::AttachEngine3D
  FirstAngle = 0
  Height = 12
  Placement = pos=(73,26,141) rot=(0,0.707107,-0.707107;3.14159rad)
  Radius = 5.5
  SecondAngle = 0
FEATURE [Part::Cylinder] Cylinder089  label="m4HoleBaseCut002"
  Angle = 360
  AttacherType = Attacher::AttachEngine3D
  FirstAngle = 0
  Height = 7
  Placement = pos=(73,26,141) rot=(0,0.707107,-0.707107;3.14159rad)
  Radius = 3.75
  SecondAngle = 0
FEATURE [Part::Cylinder] Cylinder090  label="m4HoleBase009"
  Angle = 360
  AttacherType = Attacher::AttachEngine3D
  FirstAngle = 0
  Height = 12
  Placement = pos=(5,26,141) rot=(0,0.707107,-0.707107;3.14159rad)
  Radius = 5.5
  SecondAngle = 0
FEATURE [Part::Cylinder] Cylinder091  label="m4HoleBaseCut003"
  Angle = 360
  AttacherType = Attacher::AttachEngine3D
  FirstAngle = 0
  Height = 7
  Placement = pos=(5,26,141) rot=(0,0.707107,-0.707107;3.14159rad)
  Radius = 3.75
  SecondAngle = 0
FEATURE [Part::Cylinder] Cylinder092  label="m4HoleBaseCut004"
  Angle = 360
  AttacherType = Attacher::AttachEngine3D
  FirstAngle = 0
  Height = 7
  Placement = pos=(73,26,5) rot=(0,0.707107,-0.707107;3.14159rad)
  Radius = 2.1
  SecondAngle = 0
FEATURE [Part::Cylinder] Cylinder093  label="m4HoleBaseCut005"
  Angle = 360
  AttacherType = Attacher::AttachEngine3D
  FirstAngle = 0
  Height = 7
  Placement = pos=(5,26,5) rot=(0,0.707107,-0.707107;3.14159rad)
  Radius = 2.1
  SecondAngle = 0
FEATURE [Part::Cylinder] Cylinder094  label="m4HoleBaseCut006"
  Angle = 360
  AttacherType = Attacher::AttachEngine3D
  FirstAngle = 0
  Height = 7
  Placement = pos=(73,26,141) rot=(0,0.707107,-0.707107;3.14159rad)
  Radius = 2.1
  SecondAngle = 0
FEATURE [Part::Cylinder] Cylinder095  label="m4HoleBaseCut007"
  Angle = 360
  AttacherType = Attacher::AttachEngine3D
  FirstAngle = 0
  Height = 7
  Placement = pos=(5,26,141) rot=(0,0.707107,-0.707107;3.14159rad)
  Radius = 2.1
  SecondAngle = 0
FEATURE [Part::Cylinder] Cylinder096
  Angle = 360
  AttacherType = Attacher::AttachEngine3D
  FirstAngle = 0
  Height = 20
  Radius = 6
  SecondAngle = 0
FEATURE [Part::Cylinder] Cylinder097
  Angle = 360
  AttacherType = Attacher::AttachEngine3D
  FirstAngle = 0
  Height = 5
  Radius = 10
  SecondAngle = 0
FEATURE [Part::Cylinder] Cylinder098  label="Ethernet"
  Angle = 360
  AttacherType = Attacher::AttachEngine3D
  FirstAngle = 0
  Height = 36
  Radius = 10.5
  SecondAngle = 0
FEATURE [Part::Cylinder] Cylinder099  label="Ethernet001"
  Angle = 360
  AttacherType = Attacher::AttachEngine3D
  FirstAngle = 0
  Height = 2.25
  Placement = pos=(0,0,13.5) rot=(0,0,1;0rad)
  Radius = 15
  SecondAngle = 0
FEATURE [Part::Cylinder] Cylinder102  label="hookReinforment"
  Angle = 90
  AttacherType = Attacher::AttachEngine3D
  FirstAngle = 0
  Height = 60
  Placement = pos=(9,24,146) rot=(0.57735,-0.57735,0.57735;4.18879rad)
  Radius = 5
  SecondAngle = 0
FEATURE [Part::Cylinder] Cylinder105
  Angle = 360
  AttacherType = Attacher::AttachEngine3D
  FirstAngle = 0
  Height = 2
  Placement = pos=(6,0,44) rot=(0,0.707107,0.707107;3.14159rad)
  Radius = 3
  SecondAngle = 0
FEATURE [Part::Cylinder] Cylinder106
  Angle = 360
  AttacherType = Attacher::AttachEngine3D
  FirstAngle = 0
  Height = 2
  Placement = pos=(6,1.2e-14,56) rot=(0,0.707107,0.707107;3.14159rad)
  Radius = 3
  SecondAngle = 0
FEATURE [Part::Cylinder] Cylinder109
  Angle = 360
  AttacherType = Attacher::AttachEngine3D
  FirstAngle = 0
  Height = 78
  Placement = pos=(-6.8e-15,11.4,30.7) rot=(0,1,0;1.5708rad)
  Radius = 12.5
  SecondAngle = 0
FEATURE [Part::Cut] Cut056
  Base = -> Box071
  Tool = -> Cylinder109
FEATURE [Part::Cylinder] Cylinder110  label="m4SupportDisk001"
  Angle = 360
  AttacherType = Attacher::AttachEngine3D
  FirstAngle = 0
  Height = 15
  Placement = pos=(5,-20.09,141) rot=(-1,0,0;1.5708rad)
  Radius = 5.69
  SecondAngle = 0
FEATURE [Part::Cut] Cut057
  Base = -> Clone001
  Placement = pos=(0,0.5,0) rot=(0,0,1;0rad)
  Tool = -> Cylinder110
FEATURE [Part::Cylinder] Cylinder111  label="m4HoleBaseCut008"
  Angle = 360
  AttacherType = Attacher::AttachEngine3D
  FirstAngle = 0
  Height = 79
  Placement = pos=(5,26,141) rot=(0,0.707107,-0.707107;3.14159rad)
  Radius = 2.1
  SecondAngle = 0
FEATURE [Part::Cylinder] Cylinder112  label="m4SupportDisk002"
  Angle = 360
  AttacherType = Attacher::AttachEngine3D
  FirstAngle = 0
  Height = 15
  Placement = pos=(5,-25,141) rot=(-1,0,0;1.5708rad)
  Radius = 5.69
  SecondAngle = 0
FEATURE [Part::Cylinder] Cylinder113  label="m4SupportDisk003"
  Angle = 360
  AttacherType = Attacher::AttachEngine3D
  FirstAngle = 0
  Height = 15
  Placement = pos=(5,-20.09,141) rot=(-1,0,0;1.5708rad)
  Radius = 5.69
  SecondAngle = 0
FEATURE [Part::Cut] Cut060
  Base = -> Clone002
  Placement = pos=(0,0.5,0) rot=(0,0,1;0rad)
  Tool = -> Cylinder113
FEATURE [Part::Cylinder] Cylinder114  label="m4HoleBaseCut009"
  Angle = 360
  AttacherType = Attacher::AttachEngine3D
  FirstAngle = 0
  Height = 79
  Placement = pos=(5,26,141) rot=(0,0.707107,-0.707107;3.14159rad)
  Radius = 2.1
  SecondAngle = 0
FEATURE [Part::Cylinder] Cylinder115  label="m4SupportDisk004"
  Angle = 360
  AttacherType = Attacher::AttachEngine3D
  FirstAngle = 0
  Height = 15
  Placement = pos=(5,-25,141) rot=(-1,0,0;1.5708rad)
  Radius = 5.69
  SecondAngle = 0
FEATURE [Part::Cylinder] Cylinder116  label="m4SupportDisk005"
  Angle = 360
  AttacherType = Attacher::AttachEngine3D
  FirstAngle = 0
  Height = 15
  Placement = pos=(5,-20.09,141) rot=(-1,0,0;1.5708rad)
  Radius = 5.69
  SecondAngle = 0
FEATURE [Part::Cut] Cut063
  Base = -> Clone003
  Placement = pos=(0,0.5,0) rot=(0,0,1;0rad)
  Tool = -> Cylinder116
FEATURE [Part::Cylinder] Cylinder117  label="m4HoleBaseCut010"
  Angle = 360
  AttacherType = Attacher::AttachEngine3D
  FirstAngle = 0
  Height = 79
  Placement = pos=(5,26,141) rot=(0,0.707107,-0.707107;3.14159rad)
  Radius = 2.1
  SecondAngle = 0
FEATURE [Part::Cylinder] Cylinder118  label="m4SupportDisk006"
  Angle = 360
  AttacherType = Attacher::AttachEngine3D
  FirstAngle = 0
  Height = 15
  Placement = pos=(5,-25,141) rot=(-1,0,0;1.5708rad)
  Radius = 5.69
  SecondAngle = 0
FEATURE [Part::Cylinder] Cylinder119  label="m4SupportDisk007"
  Angle = 360
  AttacherType = Attacher::AttachEngine3D
  FirstAngle = 0
  Height = 15
  Placement = pos=(5,-20.09,141) rot=(-1,0,0;1.5708rad)
  Radius = 5.69
  SecondAngle = 0
FEATURE [Part::Cut] Cut066
  Base = -> Clone004
  Placement = pos=(0,0.5,0) rot=(0,0,1;0rad)
  Tool = -> Cylinder119
FEATURE [Part::Cylinder] Cylinder120  label="m4HoleBaseCut011"
  Angle = 360
  AttacherType = Attacher::AttachEngine3D
  FirstAngle = 0
  Height = 79
  Placement = pos=(5,26,141) rot=(0,0.707107,-0.707107;3.14159rad)
  Radius = 2.1
  SecondAngle = 0
FEATURE [Part::Cylinder] Cylinder122  label="m4SupportDisk009"
  Angle = 360
  AttacherType = Attacher::AttachEngine3D
  FirstAngle = 0
  Height = 15
  Placement = pos=(5,-20.09,141) rot=(-1,0,0;1.5708rad)
  Radius = 5.69
  SecondAngle = 0
FEATURE [Part::Cut] Cut070
  Base = -> Clone006
  Placement = pos=(0,0.5,0) rot=(0,0,1;0rad)
  Tool = -> Cylinder122
FEATURE [Part::Cylinder] Cylinder123  label="m4SupportDisk010"
  Angle = 360
  AttacherType = Attacher::AttachEngine3D
  FirstAngle = 0
  Height = 15
  Placement = pos=(5,-20.09,141) rot=(-1,0,0;1.5708rad)
  Radius = 5.69
  SecondAngle = 0
FEATURE [Part::Cut] Cut071
  Base = -> Clone007
  Placement = pos=(0,0.5,0) rot=(0,0,1;0rad)
  Tool = -> Cylinder123
FEATURE [Part::Cylinder] Cylinder124  label="m4SupportDisk011"
  Angle = 360
  AttacherType = Attacher::AttachEngine3D
  FirstAngle = 0
  Height = 15
  Placement = pos=(5,-20.09,141) rot=(-1,0,0;1.5708rad)
  Radius = 5.69
  SecondAngle = 0
FEATURE [Part::Cut] Cut072
  Base = -> Clone008
  Placement = pos=(0,0.5,0) rot=(0,0,1;0rad)
  Tool = -> Cylinder124
FEATURE [Part::Cylinder] Cylinder125  label="m4SupportDisk012"
  Angle = 360
  AttacherType = Attacher::AttachEngine3D
  FirstAngle = 0
  Height = 15
  Placement = pos=(5,-20.09,141) rot=(-1,0,0;1.5708rad)
  Radius = 5.69
  SecondAngle = 0
FEATURE [Part::Cut] Cut073
  Base = -> Clone009
  Placement = pos=(0,0.5,0) rot=(0,0,1;0rad)
  Tool = -> Cylinder125
FEATURE [Part::Cylinder] Cylinder126
  Angle = 180
  AttacherType = Attacher::AttachEngine3D
  FirstAngle = 0
  Height = 82
  Placement = pos=(0,5,5) rot=(0.707107,0,0.707107;3.14159rad)
  Radius = 5
  SecondAngle = 0
FEATURE [Part::Cut] Cut078  label="cornerCuts002"
  Base = -> Box075
  Tool = -> Cylinder126
FEATURE [Part::Cylinder] Cylinder127
  Angle = 180
  AttacherType = Attacher::AttachEngine3D
  FirstAngle = 0
  Height = 82
  Placement = pos=(0,5,5) rot=(0.707107,0,0.707107;3.14159rad)
  Radius = 5
  SecondAngle = 0
FEATURE [Part::Cut] Cut079  label="cornerCuts003"
  Base = -> Box076
  Placement = pos=(0,20,10) rot=(1,0,0;3.14159rad)
  Tool = -> Cylinder127
FEATURE [Part::Cylinder] Cylinder128
  Angle = 180
  AttacherType = Attacher::AttachEngine3D
  FirstAngle = 0
  Height = 82
  Placement = pos=(0,5,5) rot=(0.707107,0,0.707107;3.14159rad)
  Radius = 5
  SecondAngle = 0
FEATURE [Part::Cut] Cut082  label="cornerCuts004"
  Base = -> Box078
  Tool = -> Cylinder128
FEATURE [Part::Cylinder] Cylinder129
  Angle = 180
  AttacherType = Attacher::AttachEngine3D
  FirstAngle = 0
  Height = 82
  Placement = pos=(0,5,5) rot=(0.707107,0,0.707107;3.14159rad)
  Radius = 5
  SecondAngle = 0
FEATURE [Part::Cut] Cut083  label="cornerCuts005"
  Base = -> Box079
  Placement = pos=(0,20,10) rot=(1,0,0;3.14159rad)
  Tool = -> Cylinder129
FEATURE [Part::Cylinder] Cylinder130
  Angle = 360
  AttacherType = Attacher::AttachEngine3D
  FirstAngle = 0
  Height = 20
  Radius = 6
  SecondAngle = 0
FEATURE [Part::Cylinder] Cylinder131
  Angle = 360
  AttacherType = Attacher::AttachEngine3D
  FirstAngle = 0
  Height = 5
  Radius = 7
  SecondAngle = 0
FEATURE [Part::Cylinder] Cylinder132
  Angle = 360
  AttacherType = Attacher::AttachEngine3D
  FirstAngle = 0
  Height = 8
  Placement = pos=(13.5,-2,3.5) rot=(1,0,0;1.5708rad)
  Radius = 1.6
  SecondAngle = 0
FEATURE [Part::Cylinder] Cylinder133
  Angle = 360
  AttacherType = Attacher::AttachEngine3D
  FirstAngle = 0
  Height = 8
  Placement = pos=(62.5,-2,3.5) rot=(1,0,0;1.5708rad)
  Radius = 1.6
  SecondAngle = 0
FEATURE [Part::Cylinder] Cylinder134
  Angle = 360
  AttacherType = Attacher::AttachEngine3D
  FirstAngle = 0
  Height = 20
  Radius = 6
  SecondAngle = 0
FEATURE [Part::Cylinder] Cylinder135
  Angle = 360
  AttacherType = Attacher::AttachEngine3D
  FirstAngle = 0
  Height = 5
  Radius = 7
  SecondAngle = 0
FEATURE [Part::MultiFuse] Fusion005
  Placement = pos=(0,-2,0) rot=(0,0,1;0rad)
  Shapes = -> [Cut006,Cut007,Cut008,Cut009]
FEATURE [Part::Cut] Cut010  label="BaseOut"
  Base = -> Box010
  Tool = -> Fusion005
FEATURE [Part::MultiFuse] Fusion006
  Shapes = -> [Cut012,Cut013,Cut014,Cut015]
FEATURE [Part::Cut] Cut016  label="BaseOut001"
  Base = -> Box015
  Placement = pos=(-2,-2,2) rot=(0,0,1;0rad)
  Tool = -> Fusion006
FEATURE [Part::Cut] Cut017  label="baseOut"
  Base = -> Cut010
  Tool = -> Cut016
FEATURE [Part::MultiFuse] Fusion007  label="powerSwitch"
  Placement = pos=(71,7.5,14) rot=(0,-1,0;1.5708rad)
  Shapes = -> [Cylinder025,Cylinder026]
FEATURE [Part::MultiFuse] Fusion008  label="base"
  Shapes = -> [Cut017,Cut018,Cut019,Cut020,Cut021]
FEATURE [Part::MultiFuse] Fusion009  label="base001"
  Shapes = -> [Cylinder021,Cylinder023,Box023,Box024,Box025,Fusion008]
FEATURE [Part::MultiFuse] Fusion010  label="baseCuts"
  Shapes = -> [Cylinder024,Cylinder022,Fusion007]
FEATURE [Part::Cut] Cut022  label="base002"
  Base = -> Fusion009
  Tool = -> Fusion010
FEATURE [Part::MultiFuse] Fusion011  label="baseCuts001"
  Placement = pos=(0,10,0) rot=(0,0,1;0rad)
  Shapes = -> [Cylinder029,Cylinder030]
FEATURE [Part::MultiFuse] Fusion012
  Placement = pos=(0,-16,0) rot=(0,0,1;0rad)
  Shapes = -> [Cylinder028,Cylinder027]
FEATURE [Part::MultiFuse] Fusion013  label="base003"
  Shapes = -> [Cut022,Fusion012]
FEATURE [Part::Cut] Cut023  label="baseBottom"
  Base = -> Fusion013
  Tool = -> Fusion011
FEATURE [Part::MultiFuse] Fusion017
  Placement = pos=(0,-2,0) rot=(0,0,1;0rad)
  Shapes = -> [Cut025,Cut026,Cut027,Cut028]
FEATURE [Part::Cut] Cut029  label="BaseOut002"
  Base = -> Box029
  Tool = -> Fusion017
FEATURE [Part::MultiFuse] Fusion018
  Shapes = -> [Cut030,Cut031,Cut032,Cut033]
FEATURE [Part::Cut] Cut034  label="BaseOut003"
  Base = -> Box034
  Placement = pos=(-2,-2,2) rot=(0,0,1;0rad)
  Tool = -> Fusion018
FEATURE [Part::Cut] Cut035  label="baseTop"
  Base = -> Cut029
  Placement = pos=(78,-20,0) rot=(0,0,1;3.14159rad)
  Tool = -> Cut034
FEATURE [Part::MultiFuse] Fusion019  label="baseTop001"
  Shapes = -> [Cut036,Cut037,Cylinder052,Cylinder053,Cut035]
FEATURE [Part::MultiFuse] Fusion020  label="baseTop002"
  Shapes = -> [Cylinder069,Cylinder063,Cylinder064,Cylinder065,Cylinder066,Cylinder067,Cylinder068,Fusion019]
FEATURE [Part::MultiFuse] Fusion021  label="m2HeatSetCuts"
  Shapes = -> [Cylinder062,Cylinder054,Cylinder055,Cylinder056,Cylinder057,Cylinder058,Cylinder059,Cylinder060,Cylinder061]
FEATURE [Part::Cut] Cut038  label="baseTop003"
  Base = -> Fusion020
  Tool = -> Fusion021
FEATURE [Part::MultiFuse] Fusion025  label="baseBottom001"
  Shapes = -> [Cylinder084,Cylinder086,Cylinder088,Cylinder090,Cut023]
FEATURE [Part::MultiFuse] Fusion026  label="m4Cuts"
  Shapes = -> [Cylinder085,Cylinder087,Cylinder089,Cylinder091]
FEATURE [Part::Cut] Cut044  label="baseBottom002"
  Base = -> Fusion025
  Tool = -> Fusion026
FEATURE [Part::MultiFuse] Fusion027  label="m4Cuts001"
  Placement = pos=(0,-5,0) rot=(0,0,1;0rad)
  Shapes = -> [Cylinder092,Cylinder093,Cylinder094,Cylinder095]
FEATURE [Part::Cut] Cut045  label="baseBottom003"
  Base = -> Cut044
  Tool = -> Fusion027
FEATURE [Part::MultiFuse] Fusion028  label="Switch"
  Placement = pos=(83,7.5,14) rot=(0,-1,0;1.5708rad)
  Shapes = -> [Cylinder096,Cylinder097]
FEATURE [Part::MultiFuse] Fusion029  label="EthenetCut"
  Placement = pos=(34,5,124.5) rot=(0,-1,0;1.5708rad)
  Shapes = -> [Cylinder098,Cylinder099]
FEATURE [Part::MultiFuse] Fusion031  label="baseBottom004"
  Shapes = -> [Cut045,Box038]
FEATURE [Part::MultiFuse] Fusion032  label="baseBottom005"
  Shapes = -> [Fusion031,Cylinder102]
FEATURE [Part::MultiFuse] Fusion035  label="voltaicCut"
  Placement = pos=(33,24,31.5) rot=(0,0,1;0rad)
  Shapes = -> [Cylinder106,Cylinder105,Box042]
FEATURE [Part::MultiFuse] Fusion036
  Placement = pos=(-4,-10,15) rot=(0,0,1;0rad)
  Shapes = -> [Box045,Box046,Box047,Box048,Box049,Box050,Box051,Box052,Box053,Box054,Box055]
FEATURE [Part::MultiFuse] Fusion037
  Placement = pos=(82,0,15) rot=(0,0,1;3.14159rad)
  Shapes = -> [Box056,Box057,Box058,Box059,Box060,Box061,Box062,Box063,Box064,Box065,Box066]
FEATURE [Part::MultiFuse] Fusion038  label="vents"
  Placement = pos=(0,-32,0) rot=(0,0,1;0rad)
  Shapes = -> [Fusion036,Fusion037]
FEATURE [Part::MultiFuse] Fusion042  label="baseBottom007"
  Shapes = -> [Cut056,Box070]
FEATURE [Part::MultiFuse] Fusion058  label="topCuts"
  Shapes = -> [Fusion038,Box043]
FEATURE [Part::MultiFuse] Fusion061
  Shapes = -> [Cut078,Cut079]
FEATURE [Part::Cut] Cut080  label="usbCut003"
  Base = -> Box074
  Placement = pos=(-50,16,68) rot=(1,0,0;1.5708rad)
  Tool = -> Fusion061
FEATURE [Part::MultiFuse] Fusion062
  Shapes = -> [Cut082,Cut083]
FEATURE [Part::Cut] Cut084  label="usbCut005"
  Base = -> Box077
  Placement = pos=(50,17,68) rot=(1,0,0;1.5708rad)
  Tool = -> Fusion062
FEATURE [Part::MultiFuse] Fusion063  label="bottomCuts"
  Shapes = -> [Cut080,Cut084,Fusion035]
FEATURE [Part::MultiFuse] Fusion083  label="Switch001"
  Placement = pos=(82,7.5,14) rot=(0,-1,0;1.5708rad)
  Shapes = -> [Cylinder130,Cylinder131]
FEATURE [Part::MultiFuse] Fusion088  label="powerSwitch002"
  Placement = pos=(71,7.5,14) rot=(0,-1,0;1.5708rad)
  Shapes = -> [Cylinder134,Cylinder135]
FEATURE [Part::MultiFuse] Fusion089  label="baseCuts002"
  Shapes = -> [Cylinder133,Cylinder132,Fusion088]
FEATURE [Part::Feature] Part__Feature009  label="m3Nut"
  Placement = pos=(2.5,8,100.5) rot=(1,0,0;1.5708rad)
  shape: bbox 6.352 x 1.801 x 6.352 mm, 26 faces (baked)
FEATURE [Part::Feature] Part__Feature010  label="m3Nut001"
  Placement = pos=(2.5,7,100.5) rot=(1,0,0;1.5708rad)
  shape: bbox 6.352 x 1.801 x 6.352 mm, 26 faces (baked)
FEATURE [Part::Feature] Part__Feature011  label="m3Nut002"
  Placement = pos=(2.5,6,100.5) rot=(1,0,0;1.5708rad)
  shape: bbox 6.352 x 1.801 x 6.352 mm, 26 faces (baked)
FEATURE [Part::MultiFuse] Fusion064  label="m3Cuts"
  Shapes = -> [Part__Feature011,Part__Feature009,Part__Feature010]
FEATURE [Part::Feature] Part__Feature012  label="m3Nut003"
  Placement = pos=(2.5,8,100.5) rot=(1,0,0;1.5708rad)
  shape: bbox 6.352 x 1.801 x 6.352 mm, 26 faces (baked)
FEATURE [Part::Feature] Part__Feature013  label="m3Nut004"
  Placement = pos=(2.5,7,100.5) rot=(1,0,0;1.5708rad)
  shape: bbox 6.352 x 1.801 x 6.352 mm, 26 faces (baked)
FEATURE [Part::Feature] Part__Feature014  label="m3Nut005"
  Placement = pos=(2.5,6,100.5) rot=(1,0,0;1.5708rad)
  shape: bbox 6.352 x 1.801 x 6.352 mm, 26 faces (baked)
FEATURE [Part::MultiFuse] Fusion065  label="m3Cuts001"
  Placement = pos=(73,0,0) rot=(0,0,1;0rad)
  Shapes = -> [Part__Feature014,Part__Feature012,Part__Feature013]
FEATURE [Part::MultiFuse] Fusion066
  Shapes = -> [Fusion065,Fusion064]
FEATURE [Part::Feature] Part__Feature015  label="m3Nut006"
  Placement = pos=(2.5,8,100.5) rot=(1,0,0;1.5708rad)
  shape: bbox 6.352 x 1.801 x 6.352 mm, 26 faces (baked)
FEATURE [Part::Feature] Part__Feature016  label="m3Nut007"
  Placement = pos=(2.5,7,100.5) rot=(1,0,0;1.5708rad)
  shape: bbox 6.352 x 1.801 x 6.352 mm, 26 faces (baked)
FEATURE [Part::Feature] Part__Feature017  label="m3Nut008"
  Placement = pos=(2.5,6,100.5) rot=(1,0,0;1.5708rad)
  shape: bbox 6.352 x 1.801 x 6.352 mm, 26 faces (baked)
FEATURE [Part::MultiFuse] Fusion067  label="m3Cuts002"
  Shapes = -> [Part__Feature017,Part__Feature015,Part__Feature016]
FEATURE [Part::Feature] Part__Feature018  label="m3Nut009"
  Placement = pos=(2.5,8,100.5) rot=(1,0,0;1.5708rad)
  shape: bbox 6.352 x 1.801 x 6.352 mm, 26 faces (baked)
FEATURE [Part::Feature] Part__Feature019  label="m3Nut010"
  Placement = pos=(2.5,7,100.5) rot=(1,0,0;1.5708rad)
  shape: bbox 6.352 x 1.801 x 6.352 mm, 26 faces (baked)
FEATURE [Part::Feature] Part__Feature020  label="m3Nut011"
  Placement = pos=(2.5,6,100.5) rot=(1,0,0;1.5708rad)
  shape: bbox 6.352 x 1.801 x 6.352 mm, 26 faces (baked)
FEATURE [Part::MultiFuse] Fusion068  label="m3Cuts003"
  Placement = pos=(73,0,0) rot=(0,0,1;0rad)
  Shapes = -> [Part__Feature020,Part__Feature018,Part__Feature019]
FEATURE [Part::MultiFuse] Fusion069
  Placement = pos=(0,2,0) rot=(0,0,1;0rad)
  Shapes = -> [Fusion068,Fusion067]
FEATURE [Part::MultiFuse] Fusion070  label="m3Cuts004"
  Shapes = -> [Fusion066,Fusion069]
FEATURE [Part::Feature] Part__Feature021  label="m3Nut012"
  Placement = pos=(2.5,8,100.5) rot=(1,0,0;1.5708rad)
  shape: bbox 6.352 x 1.801 x 6.352 mm, 26 faces (baked)
FEATURE [Part::Feature] Part__Feature022  label="m3Nut013"
  Placement = pos=(2.5,7,100.5) rot=(1,0,0;1.5708rad)
  shape: bbox 6.352 x 1.801 x 6.352 mm, 26 faces (baked)
FEATURE [Part::Feature] Part__Feature023  label="m3Nut014"
  Placement = pos=(2.5,6,100.5) rot=(1,0,0;1.5708rad)
  shape: bbox 6.352 x 1.801 x 6.352 mm, 26 faces (baked)
FEATURE [Part::MultiFuse] Fusion071  label="m3Cuts005"
  Shapes = -> [Part__Feature023,Part__Feature021,Part__Feature022]
FEATURE [Part::Feature] Part__Feature024  label="m3Nut018"
  Placement = pos=(2.5,8,100.5) rot=(1,0,0;1.5708rad)
  shape: bbox 6.352 x 1.801 x 6.352 mm, 26 faces (baked)
FEATURE [Part::Feature] Part__Feature025  label="m3Nut019"
  Placement = pos=(2.5,7,100.5) rot=(1,0,0;1.5708rad)
  shape: bbox 6.352 x 1.801 x 6.352 mm, 26 faces (baked)
FEATURE [Part::Feature] Part__Feature026  label="m3Nut020"
  Placement = pos=(2.5,6,100.5) rot=(1,0,0;1.5708rad)
  shape: bbox 6.352 x 1.801 x 6.352 mm, 26 faces (baked)
FEATURE [Part::MultiFuse] Fusion074  label="m3Cuts007"
  Placement = pos=(0,-3,0) rot=(0,0,1;0rad)
  Shapes = -> [Part__Feature026,Part__Feature024,Part__Feature025]
FEATURE [Part::MultiFuse] Fusion075  label="m3Cuts008"
  Placement = pos=(11,-7,-97) rot=(0,0,1;0rad)
  Shapes = -> [Fusion071,Fusion074]
FEATURE [Part::Feature] Part__Feature027  label="m3Nut021"
  Placement = pos=(2.5,8,100.5) rot=(1,0,0;1.5708rad)
  shape: bbox 6.352 x 1.801 x 6.352 mm, 26 faces (baked)
FEATURE [Part::Feature] Part__Feature028  label="m3Nut022"
  Placement = pos=(2.5,7,100.5) rot=(1,0,0;1.5708rad)
  shape: bbox 6.352 x 1.801 x 6.352 mm, 26 faces (baked)
FEATURE [Part::Feature] Part__Feature029  label="m3Nut023"
  Placement = pos=(2.5,6,100.5) rot=(1,0,0;1.5708rad)
  shape: bbox 6.352 x 1.801 x 6.352 mm, 26 faces (baked)
FEATURE [Part::MultiFuse] Fusion076  label="m3Cuts009"
  Shapes = -> [Part__Feature029,Part__Feature027,Part__Feature028]
FEATURE [Part::Feature] Part__Feature030  label="m3Nut024"
  Placement = pos=(2.5,8,100.5) rot=(1,0,0;1.5708rad)
  shape: bbox 6.352 x 1.801 x 6.352 mm, 26 faces (baked)
FEATURE [Part::Feature] Part__Feature031  label="m3Nut025"
  Placement = pos=(2.5,7,100.5) rot=(1,0,0;1.5708rad)
  shape: bbox 6.352 x 1.801 x 6.352 mm, 26 faces (baked)
FEATURE [Part::Feature] Part__Feature032  label="m3Nut026"
  Placement = pos=(2.5,6,100.5) rot=(1,0,0;1.5708rad)
  shape: bbox 6.352 x 1.801 x 6.352 mm, 26 faces (baked)
FEATURE [Part::MultiFuse] Fusion077  label="m3Cuts010"
  Placement = pos=(0,-3,0) rot=(0,0,1;0rad)
  Shapes = -> [Part__Feature032,Part__Feature030,Part__Feature031]
FEATURE [Part::MultiFuse] Fusion078  label="m3Cuts011"
  Placement = pos=(60,-7,-97) rot=(0,0,1;0rad)
  Shapes = -> [Fusion076,Fusion077]
FEATURE [Part::MultiFuse] Fusion079
  Shapes = -> [Fusion075,Fusion078]
FEATURE [Part::MultiFuse] Fusion080  label="bottomCuts001"
  Shapes = -> [Fusion063,Fusion079]
FEATURE [Part::MultiFuse] Fusion081  label="bottomCuts002"
  Shapes = -> [Fusion070,Fusion080]
FEATURE [Part::MultiFuse] Fusion084  label="bottomCuts003"
  Shapes = -> [Fusion083,Fusion081]
FEATURE [Part::Feature] Solid008  label="m4Nut"
  Placement = pos=(5,-19,141) rot=(-1,0,0;1.5708rad)
  shape: bbox 8.084 x 2.201 x 8.084 mm, 26 faces (baked)
FEATURE [Part::MultiFuse] Fusion044
  Shapes = -> [Cut057,Solid008]
FEATURE [Part::Cut] Cut058  label="m4Hold"
  Base = -> Cylinder073
  Tool = -> Fusion044
FEATURE [Part::Cut] Cut059  label="m4Hold001"
  Base = -> Cut058
  Tool = -> Cylinder111
FEATURE [Part::Feature] Solid009  label="m4Nut004"
  Placement = pos=(5,-19,141) rot=(-1,0,0;1.5708rad)
  shape: bbox 8.084 x 2.201 x 8.084 mm, 26 faces (baked)
FEATURE [Part::MultiFuse] Fusion045
  Shapes = -> [Cut060,Solid009]
FEATURE [Part::Cut] Cut061  label="m4Hold002"
  Base = -> Cylinder112
  Tool = -> Fusion045
FEATURE [Part::Cut] Cut062  label="m4Hold003"
  Base = -> Cut061
  Placement = pos=(68,0,0) rot=(0,0,1;0rad)
  Tool = -> Cylinder114
FEATURE [Part::Feature] Solid010  label="m4Nut006"
  Placement = pos=(5,-19,141) rot=(-1,0,0;1.5708rad)
  shape: bbox 8.084 x 2.201 x 8.084 mm, 26 faces (baked)
FEATURE [Part::MultiFuse] Fusion046
  Shapes = -> [Cut063,Solid010]
FEATURE [Part::Cut] Cut064  label="m4Hold004"
  Base = -> Cylinder115
  Tool = -> Fusion046
FEATURE [Part::Cut] Cut065  label="m4Hold005"
  Base = -> Cut064
  Placement = pos=(68,0,-136) rot=(0,0,1;0rad)
  Tool = -> Cylinder117
FEATURE [Part::Feature] Solid011  label="m4Nut008"
  Placement = pos=(5,-19,141) rot=(-1,0,0;1.5708rad)
  shape: bbox 8.084 x 2.201 x 8.084 mm, 26 faces (baked)
FEATURE [Part::MultiFuse] Fusion047
  Shapes = -> [Cut066,Solid011]
FEATURE [Part::Cut] Cut067  label="m4Hold006"
  Base = -> Cylinder118
  Tool = -> Fusion047
FEATURE [Part::Cut] Cut068  label="m4Hold007"
  Base = -> Cut067
  Placement = pos=(0,0,-136) rot=(0,0,1;0rad)
  Tool = -> Cylinder120
FEATURE [Part::MultiFuse] Fusion048  label="m4Holds"
  Shapes = -> [Cut059,Cut062,Cut065,Cut068]
FEATURE [Part::MultiFuse] Fusion049  label="top"
  Shapes = -> [Cut038,Fusion048]
FEATURE [Part::Feature] Solid013  label="m4Nut011"
  Placement = pos=(5,-19,141) rot=(-1,0,0;1.5708rad)
  shape: bbox 8.084 x 2.201 x 8.084 mm, 26 faces (baked)
FEATURE [Part::MultiFuse] Fusion051
  Shapes = -> [Cut070,Solid013]
FEATURE [Part::Feature] Solid014  label="m4Nut014"
  Placement = pos=(5,-19,141) rot=(-1,0,0;1.5708rad)
  shape: bbox 8.084 x 2.201 x 8.084 mm, 26 faces (baked)
FEATURE [Part::MultiFuse] Fusion052
  Placement = pos=(68,0,0) rot=(0,0,1;0rad)
  Shapes = -> [Cut071,Solid014]
FEATURE [Part::MultiFuse] Fusion053
  Shapes = -> [Fusion051,Fusion052]
FEATURE [Part::Feature] Solid015  label="m4Nut017"
  Placement = pos=(5,-19,141) rot=(-1,0,0;1.5708rad)
  shape: bbox 8.084 x 2.201 x 8.084 mm, 26 faces (baked)
FEATURE [Part::MultiFuse] Fusion054
  Shapes = -> [Cut072,Solid015]
FEATURE [Part::Feature] Solid016  label="m4Nut018"
  Placement = pos=(5,-19,141) rot=(-1,0,0;1.5708rad)
  shape: bbox 8.084 x 2.201 x 8.084 mm, 26 faces (baked)
FEATURE [Part::MultiFuse] Fusion055
  Placement = pos=(68,0,0) rot=(0,0,1;0rad)
  Shapes = -> [Cut073,Solid016]
FEATURE [Part::MultiFuse] Fusion056
  Placement = pos=(0,0,-136) rot=(0,0,1;0rad)
  Shapes = -> [Fusion054,Fusion055]
FEATURE [Part::MultiFuse] Fusion057
  Placement = pos=(0,-3,0) rot=(0,0,1;0rad)
  Shapes = -> [Fusion056,Fusion053]
FEATURE [Part::Cut] Cut074  label="top001"
  Base = -> Fusion049
  Tool = -> Fusion057
FEATURE [Part::Cut] Cut075
  Base = -> Cut074
  Tool = -> Fusion058
FEATURE [Part::MultiFuse] Fusion059  label="top002"
  Shapes = -> [Cut075,Cut043]
FEATURE [Part::FeaturePython] Tube  label="hookCut"  # WARN: FeaturePython — macro-defined, semantics opaque (R4)
  AttacherType = Attacher::AttachEngine3D
  Height = 10
  InnerRadius = 5
  OuterRadius = 7
  Placement = pos=(34,24,146) rot=(0,1,0;1.5708rad)
FEATURE [Part::MultiFuse] Fusion033  label="baseBottomCuts"
  Shapes = -> [Fusion029,Fusion028,Tube]
FEATURE [Part::Cut] Cut046  label="baseBottom006"
  Base = -> Fusion032
  Tool = -> Fusion033
FEATURE [Part::MultiFuse] Fusion082  label="bottom"
  Shapes = -> [Cut046,Fusion042]
FEATURE [Part::Cut] Cut085
  Base = -> Fusion082
  Tool = -> Fusion084
FEATURE [Part::Cut] Cut086  label="bottom001"
  Base = -> Cut085
  Tool = -> Box080
FEATURE [Part::Cut] Cut088  label="bottom002"
  Base = -> Cut086
  Tool = -> Fusion089
FEATURE [Part::Feature] logo3mmWidth001_solid  label="logo3mmWidth001 (Solid)"
  shape: bbox 30 x 22.21 x 4.944 mm, 7244 faces (baked)
FEATURE [Part::MultiFuse] Fusion060
  Shapes = -> [Box072,logo3mmWidth001_solid]
FEATURE [Part::Cut] Cut076  label="logo004"
  Base = -> Fusion060
  Placement = pos=(21,-42.5,14.6) rot=(1,0,0;1.5708rad)
  Tool = -> Box073
FEATURE [Part::Cut] Cut077  label="top003"
  Base = -> Fusion059
  Tool = -> Cut076
FEATURE [Part::MultiFuse] Fusion
  Placement = pos=(96.88,1.99,-18) rot=(0,0,1;0rad)
  Shapes = -> [Cut077,Cut088]
FEATURE [Part::Box] Box081  label="Cube067"
  AttacherType = Attacher::AttachEngine3D
  Height = 10
  Length = 10
  Placement = pos=(0,-10,0) rot=(0,0,1;0rad)
  Width = 36
FEATURE [Part::Box] Box082  label="Cube068"
  AttacherType = Attacher::AttachEngine3D
  Height = 10
  Length = 10
  Placement = pos=(0,-10,0) rot=(0,0,1;0rad)
  Width = 36
FEATURE [Part::Box] Box083  label="Cube069"
  AttacherType = Attacher::AttachEngine3D
  Height = 10
  Length = 10
  Placement = pos=(0,-10,0) rot=(0,0,1;0rad)
  Width = 36
FEATURE [Part::Box] Box084  label="Cube070"
  AttacherType = Attacher::AttachEngine3D
  Height = 10
  Length = 10
  Placement = pos=(0,-10,0) rot=(0,0,1;0rad)
  Width = 36
FEATURE [Part::Cylinder] Cylinder136
  Angle = 90
  AttacherType = Attacher::AttachEngine3D
  FirstAngle = 0
  Height = 36
  Placement = pos=(0,26,-5.8e-15) rot=(1,0,0;1.5708rad)
  Radius = 10
  SecondAngle = 0
FEATURE [Part::Cut] Cut089
  Base = -> Box081
  Placement = pos=(8,6,-6) rot=(0.707107,0,-0.707107;3.14159rad)
  Tool = -> Cylinder136
FEATURE [Part::Cylinder] Cylinder137
  Angle = 90
  AttacherType = Attacher::AttachEngine3D
  FirstAngle = 0
  Height = 36
  Placement = pos=(0,26,-5.8e-15) rot=(1,0,0;1.5708rad)
  Radius = 10
  SecondAngle = 0
FEATURE [Part::Cut] Cut090
  Base = -> Box082
  Placement = pos=(70,6,-6) rot=(1,0,0;3.14159rad)
  Tool = -> Cylinder137
FEATURE [Part::Cylinder] Cylinder138
  Angle = 90
  AttacherType = Attacher::AttachEngine3D
  FirstAngle = 0
  Height = 36
  Placement = pos=(0,26,-5.8e-15) rot=(1,0,0;1.5708rad)
  Radius = 10
  SecondAngle = 0
FEATURE [Part::Cut] Cut091
  Base = -> Box083
  Placement = pos=(8,6,103) rot=(0,0,1;3.14159rad)
  Tool = -> Cylinder138
FEATURE [Part::Cylinder] Cylinder139
  Angle = 90
  AttacherType = Attacher::AttachEngine3D
  FirstAngle = 0
  Height = 36
  Placement = pos=(0,26,-5.8e-15) rot=(1,0,0;1.5708rad)
  Radius = 10
  SecondAngle = 0
FEATURE [Part::Cut] Cut092
  Base = -> Box084
  Placement = pos=(70,6,103) rot=(0.707107,0,0.707107;3.14159rad)
  Tool = -> Cylinder139
FEATURE [Part::Box] Box  label="outerLayer"
  AttacherType = Attacher::AttachEngine3D
  Height = 129
  Length = 82
  Placement = pos=(-2,-20,-16) rot=(0,0,1;0rad)
  Width = 24
FEATURE [Part::Box] Box085  label="Cube"
  AttacherType = Attacher::AttachEngine3D
  Height = 10
  Length = 10
  Width = 10
FEATURE [App::Part] NanoPi2_Board_komplett
  Group = -> [Part__Feature,Part__Feature001,microUSB,Part__Feature004,Part__Feature005,Part__Feature006,Part__Feature007,Part__Feature008,Box085]
  Origin = -> Origin001
  Placement = pos=(29,-13.5,90) rot=(1,0,0;4.71239rad)
FEATURE [Part::Box] Box086  label="innerLayer001"
  AttacherType = Attacher::AttachEngine3D
  Height = 125
  Length = 78
  Placement = pos=(0,-18,-14) rot=(0,0,1;0rad)
  Width = 22
FEATURE [Part::Box] Box087  label="Cube071"
  AttacherType = Attacher::AttachEngine3D
  Height = 10
  Length = 10
  Placement = pos=(0,-10,0) rot=(0,0,1;0rad)
  Width = 36
FEATURE [Part::Box] Box088  label="Cube072"
  AttacherType = Attacher::AttachEngine3D
  Height = 10
  Length = 10
  Placement = pos=(0,-10,0) rot=(0,0,1;0rad)
  Width = 36
FEATURE [Part::Box] Box089  label="Cube073"
  AttacherType = Attacher::AttachEngine3D
  Height = 10
  Length = 10
  Placement = pos=(0,-10,0) rot=(0,0,1;0rad)
  Width = 36
FEATURE [Part::Box] Box090  label="Cube074"
  AttacherType = Attacher::AttachEngine3D
  Height = 10
  Length = 10
  Placement = pos=(0,-10,0) rot=(0,0,1;0rad)
  Width = 36
FEATURE [Part::Cylinder] Cylinder140
  Angle = 90
  AttacherType = Attacher::AttachEngine3D
  FirstAngle = 0
  Height = 36
  Placement = pos=(0,26,-5.8e-15) rot=(1,0,0;1.5708rad)
  Radius = 10
  SecondAngle = 0
FEATURE [Part::Cut] Cut093
  Base = -> Box087
  Placement = pos=(10,6,-4) rot=(0.707107,0,-0.707107;3.14159rad)
  Tool = -> Cylinder140
FEATURE [Part::Cylinder] Cylinder141
  Angle = 90
  AttacherType = Attacher::AttachEngine3D
  FirstAngle = 0
  Height = 36
  Placement = pos=(0,26,-5.8e-15) rot=(1,0,0;1.5708rad)
  Radius = 10
  SecondAngle = 0
FEATURE [Part::Cut] Cut094
  Base = -> Box088
  Placement = pos=(68,6,-4) rot=(1,0,0;3.14159rad)
  Tool = -> Cylinder141
FEATURE [Part::Cylinder] Cylinder142
  Angle = 90
  AttacherType = Attacher::AttachEngine3D
  FirstAngle = 0
  Height = 36
  Placement = pos=(0,26,-5.8e-15) rot=(1,0,0;1.5708rad)
  Radius = 10
  SecondAngle = 0
FEATURE [Part::Cut] Cut095
  Base = -> Box089
  Placement = pos=(10,6,101) rot=(0,0,1;3.14159rad)
  Tool = -> Cylinder142
FEATURE [Part::Cylinder] Cylinder143
  Angle = 90
  AttacherType = Attacher::AttachEngine3D
  FirstAngle = 0
  Height = 36
  Placement = pos=(0,26,-5.8e-15) rot=(1,0,0;1.5708rad)
  Radius = 10
  SecondAngle = 0
FEATURE [Part::Cut] Cut096
  Base = -> Box090
  Placement = pos=(68,6,101) rot=(0.707107,0,0.707107;3.14159rad)
  Tool = -> Cylinder143
FEATURE [Part::MultiFuse] Fusion090  label="outerCuts"
  Shapes = -> [Cut089,Cut090,Cut091,Cut092]
FEATURE [Part::MultiFuse] Fusion091  label="innerCuts"
  Shapes = -> [Cut093,Cut094,Cut095,Cut096]
FEATURE [Part::Cut] Cut097  label="inner"
  Base = -> Box086
  Tool = -> Fusion091
FEATURE [Part::Cut] Cut098  label="outer"
  Base = -> Box
  Tool = -> Fusion090
FEATURE [Part::Cut] Cut099  label="top004"
  Base = -> Cut098
  Tool = -> Cut097
FEATURE [Part::Cylinder] Cylinder144  label="ipsHold"
  Angle = 180
  AttacherType = Attacher::AttachEngine3D
  FirstAngle = 0
  Height = 5
  Placement = pos=(60,-18,0) rot=(0,0,1;0rad)
  Radius = 7
  SecondAngle = 0
FEATURE [Part::Cylinder] Cylinder145  label="ipsHoldCut"
  Angle = 360
  AttacherType = Attacher::AttachEngine3D
  FirstAngle = 0
  Height = 5
  Placement = pos=(60.1,-14.6,0) rot=(0,0,1;0rad)
  Radius = 1.1
  SecondAngle = 0
FEATURE [Part::Cut] Cut100  label="topIn"
  Base = -> Cylinder144
  Tool = -> Cylinder145
FEATURE [Part::Cylinder] Cylinder146  label="m2HeatSetOut009"
  Angle = 360
  AttacherType = Attacher::AttachEngine3D
  FirstAngle = 0
  Height = 12
  Placement = pos=(8,-44,67.1) rot=(-1,0,0;1.5708rad)
  Radius = 3.5
  SecondAngle = 0
FEATURE [Part::Cylinder] Cylinder147  label="m2HeatSet012"
  Angle = 360
  AttacherType = Attacher::AttachEngine3D
  FirstAngle = 0
  Height = 12
  Placement = pos=(8,-44,67.1) rot=(-1,0,0;1.5708rad)
  Radius = 1.6
  SecondAngle = 0
FEATURE [Part::Cut] Cut101  label="m2HeatSet011"
  Base = -> Cylinder146
  Placement = pos=(1,0,-13.1) rot=(0,0,1;0rad)
  Tool = -> Cylinder147
FEATURE [Part::Cylinder] Cylinder148  label="m2HeatSetOut010"
  Angle = 360
  AttacherType = Attacher::AttachEngine3D
  FirstAngle = 0
  Height = 12
  Placement = pos=(8,-44,67.1) rot=(-1,0,0;1.5708rad)
  Radius = 3.5
  SecondAngle = 0
FEATURE [Part::Cylinder] Cylinder149  label="m2HeatSet014"
  Angle = 360
  AttacherType = Attacher::AttachEngine3D
  FirstAngle = 0
  Height = 12
  Placement = pos=(8,-44,67.1) rot=(-1,0,0;1.5708rad)
  Radius = 1.6
  SecondAngle = 0
FEATURE [Part::Cut] Cut102  label="m2HeatSet013"
  Base = -> Cylinder148
  Placement = pos=(1,0,-53.1) rot=(0,0,1;0rad)
  Tool = -> Cylinder149
FEATURE [Part::Cylinder] Cylinder152  label="m2HeatSetOut012"
  Angle = 360
  AttacherType = Attacher::AttachEngine3D
  FirstAngle = 0
  Height = 12
  Placement = pos=(8,-44,67.1) rot=(-1,0,0;1.5708rad)
  Radius = 3.5
  SecondAngle = 0
FEATURE [Part::Cylinder] Cylinder153  label="m2HeatSet018"
  Angle = 360
  AttacherType = Attacher::AttachEngine3D
  FirstAngle = 0
  Height = 12
  Placement = pos=(8,-44,67.1) rot=(-1,0,0;1.5708rad)
  Radius = 1.6
  SecondAngle = 0
FEATURE [Part::Cut] Cut104  label="m2HeatSet017"
  Base = -> Cylinder152
  Placement = pos=(31,0,-3.1) rot=(0,0,1;0rad)
  Tool = -> Cylinder153
FEATURE [Part::Cylinder] Cylinder154  label="m2HeatSetOut013"
  Angle = 360
  AttacherType = Attacher::AttachEngine3D
  FirstAngle = 0
  Height = 12
  Placement = pos=(8,-44,67.1) rot=(-1,0,0;1.5708rad)
  Radius = 3.5
  SecondAngle = 0
FEATURE [Part::Cylinder] Cylinder155  label="m2HeatSet020"
  Angle = 360
  AttacherType = Attacher::AttachEngine3D
  FirstAngle = 0
  Height = 12
  Placement = pos=(8,-44,67.1) rot=(-1,0,0;1.5708rad)
  Radius = 1.6
  SecondAngle = 0
FEATURE [Part::Cut] Cut105  label="m2HeatSet019"
  Base = -> Cylinder154
  Placement = pos=(41,0,-13.1) rot=(0,0,1;0rad)
  Tool = -> Cylinder155
FEATURE [Part::Cylinder] Cylinder160  label="m2HeatSetOut016"
  Angle = 360
  AttacherType = Attacher::AttachEngine3D
  FirstAngle = 0
  Height = 12
  Placement = pos=(8,-44,67.1) rot=(-1,0,0;1.5708rad)
  Radius = 3.5
  SecondAngle = 0
FEATURE [Part::Cylinder] Cylinder161  label="m2HeatSet026"
  Angle = 360
  AttacherType = Attacher::AttachEngine3D
  FirstAngle = 0
  Height = 12
  Placement = pos=(8,-44,67.1) rot=(-1,0,0;1.5708rad)
  Radius = 1.6
  SecondAngle = 0
FEATURE [Part::Cut] Cut108  label="m2HeatSet025"
  Base = -> Cylinder160
  Placement = pos=(61,0,-13.1) rot=(0,0,1;0rad)
  Tool = -> Cylinder161
FEATURE [Part::Cylinder] Cylinder162  label="m2HeatSetOut017"
  Angle = 360
  AttacherType = Attacher::AttachEngine3D
  FirstAngle = 0
  Height = 4.5
  Placement = pos=(8,-44,67.1) rot=(-1,0,0;1.5708rad)
  Radius = 5
  SecondAngle = 0
FEATURE [Part::Cylinder] Cylinder163  label="m2HeatSet028"
  Angle = 360
  AttacherType = Attacher::AttachEngine3D
  FirstAngle = 0
  Height = 12
  Placement = pos=(8,-44,67.1) rot=(-1,0,0;1.5708rad)
  Radius = 2
  SecondAngle = 0
FEATURE [Part::Cut] Cut109  label="m3HeatSet027"
  Base = -> Cylinder162
  Placement = pos=(3.3,0,5.2) rot=(0,0,1;0rad)
  Tool = -> Cylinder163
FEATURE [Part::Cylinder] Cylinder164  label="m2HeatSetOut018"
  Angle = 360
  AttacherType = Attacher::AttachEngine3D
  FirstAngle = 0
  Height = 4.5
  Placement = pos=(8,-44,67.1) rot=(-1,0,0;1.5708rad)
  Radius = 5
  SecondAngle = 0
FEATURE [Part::Cylinder] Cylinder165  label="m2HeatSet029"
  Angle = 360
  AttacherType = Attacher::AttachEngine3D
  FirstAngle = 0
  Height = 12
  Placement = pos=(8,-44,67.1) rot=(-1,0,0;1.5708rad)
  Radius = 2
  SecondAngle = 0
FEATURE [Part::Cut] Cut110  label="m3HeatSet028"
  Base = -> Cylinder164
  Placement = pos=(38.7,0,5.2) rot=(0,0,1;0rad)
  Tool = -> Cylinder165
FEATURE [Part::Cylinder] Cylinder166  label="m2HeatSetOut019"
  Angle = 360
  AttacherType = Attacher::AttachEngine3D
  FirstAngle = 0
  Height = 4.5
  Placement = pos=(8,-44,67.1) rot=(-1,0,0;1.5708rad)
  Radius = 5
  SecondAngle = 0
FEATURE [Part::Cylinder] Cylinder167  label="m2HeatSet030"
  Angle = 360
  AttacherType = Attacher::AttachEngine3D
  FirstAngle = 0
  Height = 12
  Placement = pos=(8,-44,67.1) rot=(-1,0,0;1.5708rad)
  Radius = 2
  SecondAngle = 0
FEATURE [Part::Cut] Cut111  label="m3HeatSet029"
  Base = -> Cylinder166
  Placement = pos=(3.3,0,40.6) rot=(0,0,1;0rad)
  Tool = -> Cylinder167
FEATURE [Part::Cylinder] Cylinder168  label="m2HeatSetOut020"
  Angle = 360
  AttacherType = Attacher::AttachEngine3D
  FirstAngle = 0
  Height = 4.5
  Placement = pos=(8,-44,67.1) rot=(-1,0,0;1.5708rad)
  Radius = 5
  SecondAngle = 0
FEATURE [Part::Cylinder] Cylinder169  label="m2HeatSet031"
  Angle = 360
  AttacherType = Attacher::AttachEngine3D
  FirstAngle = 0
  Height = 12
  Placement = pos=(8,-44,67.1) rot=(-1,0,0;1.5708rad)
  Radius = 2
  SecondAngle = 0
FEATURE [Part::Cut] Cut112  label="m3HeatSet030"
  Base = -> Cylinder168
  Placement = pos=(38.7,0,40.6) rot=(0,0,1;0rad)
  Tool = -> Cylinder169
FEATURE [Part::MultiFuse] Fusion092  label="topIn001"
  Placement = pos=(0,26,0) rot=(0,0,1;0rad)
  Shapes = -> [Cut101,Cut102,Cut104,Cut105,Cut108,Cut109,Cut110,Cut111,Cut112]
FEATURE [Part::Feature] Clone010  label="m4Nut019"
  Placement = pos=(5,-22.5,141) rot=(-1,0,0;1.5708rad)
  shape: bbox 8.083 x 8.8 x 9.333 mm, 26 faces (baked)
FEATURE [Part::Cylinder] Cylinder170  label="m4SupportDisk013"
  Angle = 360
  AttacherType = Attacher::AttachEngine3D
  FirstAngle = 0
  Height = 10
  Placement = pos=(5,-25,141) rot=(-1,0,0;1.5708rad)
  Radius = 5.69
  SecondAngle = 0
FEATURE [Part::Cylinder] Cylinder171  label="m4SupportDisk014"
  Angle = 360
  AttacherType = Attacher::AttachEngine3D
  FirstAngle = 0
  Height = 15
  Placement = pos=(5,-20.09,141) rot=(-1,0,0;1.5708rad)
  Radius = 5.69
  SecondAngle = 0
FEATURE [Part::Cut] Cut113
  Base = -> Clone010
  Placement = pos=(0,0.5,0) rot=(0,0,1;0rad)
  Tool = -> Cylinder171
FEATURE [Part::Cylinder] Cylinder172  label="m4HoleBaseCut012"
  Angle = 360
  AttacherType = Attacher::AttachEngine3D
  FirstAngle = 0
  Height = 79
  Placement = pos=(5,26,141) rot=(0,0.707107,-0.707107;3.14159rad)
  Radius = 2.1
  SecondAngle = 0
FEATURE [Part::Feature] Solid017  label="m4Nut020"
  Placement = pos=(5,-19,141) rot=(-1,0,0;1.5708rad)
  shape: bbox 8.084 x 2.201 x 8.084 mm, 26 faces (baked)
FEATURE [Part::MultiFuse] Fusion093
  Shapes = -> [Cut113,Solid017]
FEATURE [Part::Cut] Cut114  label="m4Hold008"
  Base = -> Cylinder170
  Tool = -> Fusion093
FEATURE [Part::Cut] Cut115  label="m4Hold009"
  Base = -> Cut114
  Placement = pos=(0,19,-148) rot=(0,0,1;0rad)
  Tool = -> Cylinder172
FEATURE [Part::Feature] Clone011  label="m4Nut021"
  Placement = pos=(5,-22.5,141) rot=(-1,0,0;1.5708rad)
  shape: bbox 8.083 x 8.8 x 9.333 mm, 26 faces (baked)
FEATURE [Part::Cylinder] Cylinder173  label="m4SupportDisk015"
  Angle = 360
  AttacherType = Attacher::AttachEngine3D
  FirstAngle = 0
  Height = 10
  Placement = pos=(5,-25,141) rot=(-1,0,0;1.5708rad)
  Radius = 5.69
  SecondAngle = 0
FEATURE [Part::Cylinder] Cylinder174  label="m4SupportDisk016"
  Angle = 360
  AttacherType = Attacher::AttachEngine3D
  FirstAngle = 0
  Height = 15
  Placement = pos=(5,-20.09,141) rot=(-1,0,0;1.5708rad)
  Radius = 5.69
  SecondAngle = 0
FEATURE [Part::Cut] Cut116
  Base = -> Clone011
  Placement = pos=(0,0.5,0) rot=(0,0,1;0rad)
  Tool = -> Cylinder174
FEATURE [Part::Cylinder] Cylinder175  label="m4HoleBaseCut013"
  Angle = 360
  AttacherType = Attacher::AttachEngine3D
  FirstAngle = 0
  Height = 79
  Placement = pos=(5,26,141) rot=(0,0.707107,-0.707107;3.14159rad)
  Radius = 2.1
  SecondAngle = 0
FEATURE [Part::Feature] Solid018  label="m4Nut022"
  Placement = pos=(5,-19,141) rot=(-1,0,0;1.5708rad)
  shape: bbox 8.084 x 2.201 x 8.084 mm, 26 faces (baked)
FEATURE [Part::MultiFuse] Fusion094
  Shapes = -> [Cut116,Solid018]
FEATURE [Part::Cut] Cut117  label="m4Hold010"
  Base = -> Cylinder173
  Tool = -> Fusion094
FEATURE [Part::Cut] Cut118  label="m4Hold011"
  Base = -> Cut117
  Placement = pos=(68,19,-148) rot=(0,0,1;0rad)
  Tool = -> Cylinder175
FEATURE [Part::Feature] Clone012  label="m4Nut023"
  Placement = pos=(5,-22.5,141) rot=(-1,0,0;1.5708rad)
  shape: bbox 8.083 x 8.8 x 9.333 mm, 26 faces (baked)
FEATURE [Part::Feature] Clone013  label="m4Nut024"
  Placement = pos=(5,-22.5,141) rot=(-1,0,0;1.5708rad)
  shape: bbox 8.083 x 8.8 x 9.333 mm, 26 faces (baked)
FEATURE [Part::Cylinder] Cylinder176  label="m4SupportDisk017"
  Angle = 360
  AttacherType = Attacher::AttachEngine3D
  FirstAngle = 0
  Height = 10
  Placement = pos=(5,-25,141) rot=(-1,0,0;1.5708rad)
  Radius = 5.69
  SecondAngle = 0
FEATURE [Part::Cylinder] Cylinder177  label="m4SupportDisk018"
  Angle = 360
  AttacherType = Attacher::AttachEngine3D
  FirstAngle = 0
  Height = 15
  Placement = pos=(5,-20.09,141) rot=(-1,0,0;1.5708rad)
  Radius = 5.69
  SecondAngle = 0
FEATURE [Part::Cut] Cut119
  Base = -> Clone012
  Placement = pos=(0,0.5,0) rot=(0,0,1;0rad)
  Tool = -> Cylinder177
FEATURE [Part::Cylinder] Cylinder178  label="m4HoleBaseCut014"
  Angle = 360
  AttacherType = Attacher::AttachEngine3D
  FirstAngle = 0
  Height = 79
  Placement = pos=(5,26,141) rot=(0,0.707107,-0.707107;3.14159rad)
  Radius = 2.1
  SecondAngle = 0
FEATURE [Part::Cylinder] Cylinder179  label="m4SupportDisk019"
  Angle = 360
  AttacherType = Attacher::AttachEngine3D
  FirstAngle = 0
  Height = 10
  Placement = pos=(5,-25,141) rot=(-1,0,0;1.5708rad)
  Radius = 5.69
  SecondAngle = 0
FEATURE [Part::Cylinder] Cylinder180  label="m4SupportDisk020"
  Angle = 360
  AttacherType = Attacher::AttachEngine3D
  FirstAngle = 0
  Height = 15
  Placement = pos=(5,-20.09,141) rot=(-1,0,0;1.5708rad)
  Radius = 5.69
  SecondAngle = 0
FEATURE [Part::Cut] Cut122
  Base = -> Clone013
  Placement = pos=(0,0.5,0) rot=(0,0,1;0rad)
  Tool = -> Cylinder180
FEATURE [Part::Cylinder] Cylinder181  label="m4HoleBaseCut015"
  Angle = 360
  AttacherType = Attacher::AttachEngine3D
  FirstAngle = 0
  Height = 79
  Placement = pos=(5,26,141) rot=(0,0.707107,-0.707107;3.14159rad)
  Radius = 2.1
  SecondAngle = 0
FEATURE [Part::Feature] Solid019  label="m4Nut025"
  Placement = pos=(5,-19,141) rot=(-1,0,0;1.5708rad)
  shape: bbox 8.084 x 2.201 x 8.084 mm, 26 faces (baked)
FEATURE [Part::MultiFuse] Fusion095
  Shapes = -> [Cut119,Solid019]
FEATURE [Part::Cut] Cut120  label="m4Hold012"
  Base = -> Cylinder176
  Tool = -> Fusion095
FEATURE [Part::Cut] Cut121  label="m4Hold013"
  Base = -> Cut120
  Placement = pos=(0,19,-37) rot=(0,0,1;0rad)
  Tool = -> Cylinder178
FEATURE [Part::Feature] Solid020  label="m4Nut026"
  Placement = pos=(5,-19,141) rot=(-1,0,0;1.5708rad)
  shape: bbox 8.084 x 2.201 x 8.084 mm, 26 faces (baked)
FEATURE [Part::MultiFuse] Fusion096
  Shapes = -> [Cut122,Solid020]
FEATURE [Part::Cut] Cut123  label="m4Hold014"
  Base = -> Cylinder179
  Tool = -> Fusion096
FEATURE [Part::Cut] Cut124  label="m4Hold015"
  Base = -> Cut123
  Placement = pos=(68,19,-37) rot=(0,0,1;0rad)
  Tool = -> Cylinder181
FEATURE [Part::Cylinder] Cylinder182 .. Cylinder189  x8 (patterned run collapsed; names and placements below)
  Angle = 90
  AttacherType = Attacher::AttachEngine3D
  FirstAngle = 0
  Height = 36
  Radius = 10
  SecondAngle = 0
  placements: all 8 at pos=(0,26,-5.8e-15) rot=(1,0,0;1.5708rad)
FEATURE [Part::Box] Box092  label="Cube075"
  AttacherType = Attacher::AttachEngine3D
  Height = 10
  Length = 10
  Placement = pos=(0,-10,0) rot=(0,0,1;0rad)
  Width = 36
FEATURE [Part::Box] Box093  label="Cube076"
  AttacherType = Attacher::AttachEngine3D
  Height = 10
  Length = 10
  Placement = pos=(0,-10,0) rot=(0,0,1;0rad)
  Width = 36
FEATURE [Part::Box] Box094  label="Cube077"
  AttacherType = Attacher::AttachEngine3D
  Height = 10
  Length = 10
  Placement = pos=(0,-10,0) rot=(0,0,1;0rad)
  Width = 36
FEATURE [Part::Box] Box095  label="Cube078"
  AttacherType = Attacher::AttachEngine3D
  Height = 10
  Length = 10
  Placement = pos=(0,-10,0) rot=(0,0,1;0rad)
  Width = 36
FEATURE [Part::Box] Box097  label="Cube079"
  AttacherType = Attacher::AttachEngine3D
  Height = 10
  Length = 10
  Placement = pos=(0,-10,0) rot=(0,0,1;0rad)
  Width = 36
FEATURE [Part::Box] Box098  label="Cube080"
  AttacherType = Attacher::AttachEngine3D
  Height = 10
  Length = 10
  Placement = pos=(0,-10,0) rot=(0,0,1;0rad)
  Width = 36
FEATURE [Part::Box] Box099  label="Cube081"
  AttacherType = Attacher::AttachEngine3D
  Height = 10
  Length = 10
  Placement = pos=(0,-10,0) rot=(0,0,1;0rad)
  Width = 36
FEATURE [Part::Box] Box100  label="Cube082"
  AttacherType = Attacher::AttachEngine3D
  Height = 10
  Length = 10
  Placement = pos=(0,-10,0) rot=(0,0,1;0rad)
  Width = 36
FEATURE [Part::Cut] Cut125
  Base = -> Box092
  Placement = pos=(8,6,-6) rot=(0.707107,0,-0.707107;3.14159rad)
  Tool = -> Cylinder182
FEATURE [Part::Cut] Cut126
  Base = -> Box093
  Placement = pos=(70,6,-6) rot=(1,0,0;3.14159rad)
  Tool = -> Cylinder183
FEATURE [Part::Cut] Cut127
  Base = -> Box094
  Placement = pos=(8,6,103) rot=(0,0,1;3.14159rad)
  Tool = -> Cylinder184
FEATURE [Part::Cut] Cut128
  Base = -> Box095
  Placement = pos=(70,6,103) rot=(0.707107,0,0.707107;3.14159rad)
  Tool = -> Cylinder185
FEATURE [Part::Cut] Cut129
  Base = -> Box097
  Placement = pos=(10,6,-4) rot=(0.707107,0,-0.707107;3.14159rad)
  Tool = -> Cylinder186
FEATURE [Part::Cut] Cut130
  Base = -> Box098
  Placement = pos=(68,6,-4) rot=(1,0,0;3.14159rad)
  Tool = -> Cylinder187
FEATURE [Part::Cut] Cut131
  Base = -> Box099
  Placement = pos=(10,6,101) rot=(0,0,1;3.14159rad)
  Tool = -> Cylinder188
FEATURE [Part::Cut] Cut132
  Base = -> Box100
  Placement = pos=(68,6,101) rot=(0.707107,0,0.707107;3.14159rad)
  Tool = -> Cylinder189
FEATURE [Part::MultiFuse] Fusion097  label="outerCuts001"
  Shapes = -> [Cut125,Cut126,Cut127,Cut128]
FEATURE [Part::MultiFuse] Fusion098  label="innerCuts001"
  Shapes = -> [Cut129,Cut130,Cut131,Cut132]
FEATURE [Part::Box] Box091  label="outerLayer001"
  AttacherType = Attacher::AttachEngine3D
  Height = 129
  Length = 82
  Placement = pos=(-2,-20,-16) rot=(0,0,1;0rad)
  Width = 24
FEATURE [Part::Box] Box096  label="innerLayer002"
  AttacherType = Attacher::AttachEngine3D
  Height = 125
  Length = 78
  Placement = pos=(0,-18,-14) rot=(0,0,1;0rad)
  Width = 22
FEATURE [Part::Cut] Cut133  label="inner001"
  Base = -> Box096
  Tool = -> Fusion098
FEATURE [Part::Cut] Cut134  label="outer001"
  Base = -> Box091
  Tool = -> Fusion097
FEATURE [Part::Cut] Cut135  label="bottom003"
  Base = -> Cut134
  Placement = pos=(78,8,0) rot=(0,0,1;3.14159rad)
  Tool = -> Cut133
FEATURE [Part::Box] Box101  label="Cube083"
  AttacherType = Attacher::AttachEngine3D
  Height = 10
  Length = 10
  Placement = pos=(10.5,0,-6) rot=(0,0,1;0rad)
  Width = 10
FEATURE [Part::Box] Box102  label="Cube084"
  AttacherType = Attacher::AttachEngine3D
  Height = 10
  Length = 10
  Placement = pos=(15,0,-10) rot=(0,0,1;0rad)
  Width = 10
FEATURE [Part::Cut] Cut136
  Base = -> Box101
  Tool = -> Box102
FEATURE [Part::Box] Box103  label="Cube085"
  AttacherType = Attacher::AttachEngine3D
  Height = 10
  Length = 4
  Placement = pos=(63,0,-6) rot=(0,0,1;0rad)
  Width = 10
FEATURE [Part::MultiFuse] Fusion099  label="ipsHolds"
  Placement = pos=(0,-18,0) rot=(0,0,1;0rad)
  Shapes = -> [Cut136,Box103]
FEATURE [Part::MultiFuse] Fusion100  label="m4Holds001"
  Shapes = -> [Cut115,Cut118,Cut121,Cut124]
FEATURE [Part::MultiFuse] Fusion101  label="topIn002"
  Shapes = -> [Fusion100,Fusion099]
FEATURE [Part::Box] Box104  label="Cube086"
  AttacherType = Attacher::AttachEngine3D
  Height = 10
  Length = 10
  Placement = pos=(10,26,0) rot=(0,0,1;3.14159rad)
  Width = 26
FEATURE [Part::Box] Box105  label="Cube087"
  AttacherType = Attacher::AttachEngine3D
  Height = 10
  Length = 10
  Placement = pos=(10,26,0) rot=(0,0,1;3.14159rad)
  Width = 26
FEATURE [Part::Box] Box106  label="Cube088"
  AttacherType = Attacher::AttachEngine3D
  Height = 10
  Length = 10
  Placement = pos=(10,26,0) rot=(0,0,1;3.14159rad)
  Width = 26
FEATURE [Part::Box] Box107  label="Cube089"
  AttacherType = Attacher::AttachEngine3D
  Height = 10
  Length = 10
  Placement = pos=(10,26,0) rot=(0,0,1;3.14159rad)
  Width = 26
FEATURE [Part::Cylinder] Cylinder190
  Angle = 90
  AttacherType = Attacher::AttachEngine3D
  FirstAngle = 0
  Height = 26
  Placement = pos=(0,26,-5.8e-15) rot=(1,0,0;1.5708rad)
  Radius = 10
  SecondAngle = 0
FEATURE [Part::Cut] Cut137  label="batterySupport004"
  Base = -> Box104
  Placement = pos=(10,-2,33.5) rot=(0,1,0;3.14159rad)
  Tool = -> Cylinder190
FEATURE [Part::Cylinder] Cylinder191
  Angle = 90
  AttacherType = Attacher::AttachEngine3D
  FirstAngle = 0
  Height = 26
  Placement = pos=(0,26,-5.8e-15) rot=(1,0,0;1.5708rad)
  Radius = 10
  SecondAngle = 0
FEATURE [Part::Cut] Cut138  label="batterySupport005"
  Base = -> Box105
  Placement = pos=(68,-2,33.5) rot=(0,1,0;1.5708rad)
  Tool = -> Cylinder191
FEATURE [Part::Cylinder] Cylinder192
  Angle = 90
  AttacherType = Attacher::AttachEngine3D
  FirstAngle = 0
  Height = 26
  Placement = pos=(0,26,-5.8e-15) rot=(1,0,0;1.5708rad)
  Radius = 10
  SecondAngle = 0
FEATURE [Part::Cut] Cut139  label="batterySupport006"
  Base = -> Box106
  Placement = pos=(68,-2,88) rot=(0,0,1;0rad)
  Tool = -> Cylinder192
FEATURE [Part::Cylinder] Cylinder193
  Angle = 90
  AttacherType = Attacher::AttachEngine3D
  FirstAngle = 0
  Height = 26
  Placement = pos=(0,26,-5.8e-15) rot=(1,0,0;1.5708rad)
  Radius = 10
  SecondAngle = 0
FEATURE [Part::Cut] Cut140  label="batterySupport007"
  Base = -> Box107
  Placement = pos=(10,-2,88) rot=(0,-1,0;1.5708rad)
  Tool = -> Cylinder193
FEATURE [Part::MultiFuse] Fusion102  label="bottomIn001"
  Placement = pos=(0,2,-23) rot=(0,0,1;0rad)
  Shapes = -> [Cut137,Cut138,Cut139,Cut140]
FEATURE [Part::Cylinder] Cylinder194  label="m4HoleBaseCut016"
  Angle = 360
  AttacherType = Attacher::AttachEngine3D
  FirstAngle = 0
  Height = 7
  Placement = pos=(73,26,5) rot=(0,0.707107,-0.707107;3.14159rad)
  Radius = 3.75
  SecondAngle = 0
FEATURE [Part::Cylinder] Cylinder195  label="m4HoleBaseCut017"
  Angle = 360
  AttacherType = Attacher::AttachEngine3D
  FirstAngle = 0
  Height = 7
  Placement = pos=(5,26,5) rot=(0,0.707107,-0.707107;3.14159rad)
  Radius = 3.75
  SecondAngle = 0
FEATURE [Part::Cylinder] Cylinder196  label="m4HoleBaseCut018"
  Angle = 360
  AttacherType = Attacher::AttachEngine3D
  FirstAngle = 0
  Height = 7
  Placement = pos=(73,26,116) rot=(0,0.707107,-0.707107;3.14159rad)
  Radius = 3.75
  SecondAngle = 0
FEATURE [Part::Cylinder] Cylinder197  label="m4HoleBaseCut019"
  Angle = 360
  AttacherType = Attacher::AttachEngine3D
  FirstAngle = 0
  Height = 7
  Placement = pos=(5,26,116) rot=(0,0.707107,-0.707107;3.14159rad)
  Radius = 3.75
  SecondAngle = 0
FEATURE [Part::MultiFuse] Fusion103  label="m4Cuts002"
  Placement = pos=(0,2,-12) rot=(0,0,1;0rad)
  Shapes = -> [Cylinder194,Cylinder195,Cylinder196,Cylinder197]
FEATURE [Part::Cylinder] Cylinder198  label="m4HoleBaseCut020"
  Angle = 360
  AttacherType = Attacher::AttachEngine3D
  FirstAngle = 0
  Height = 7
  Placement = pos=(73,26,30) rot=(0,0.707107,-0.707107;3.14159rad)
  Radius = 2.1
  SecondAngle = 0
FEATURE [Part::Cylinder] Cylinder199  label="m4HoleBaseCut021"
  Angle = 360
  AttacherType = Attacher::AttachEngine3D
  FirstAngle = 0
  Height = 7
  Placement = pos=(5,26,30) rot=(0,0.707107,-0.707107;3.14159rad)
  Radius = 2.1
  SecondAngle = 0
FEATURE [Part::Cylinder] Cylinder200  label="m4HoleBaseCut022"
  Angle = 360
  AttacherType = Attacher::AttachEngine3D
  FirstAngle = 0
  Height = 7
  Placement = pos=(73,26,141) rot=(0,0.707107,-0.707107;3.14159rad)
  Radius = 2.1
  SecondAngle = 0
FEATURE [Part::Cylinder] Cylinder201  label="m4HoleBaseCut023"
  Angle = 360
  AttacherType = Attacher::AttachEngine3D
  FirstAngle = 0
  Height = 7
  Placement = pos=(5,26,141) rot=(0,0.707107,-0.707107;3.14159rad)
  Radius = 2.1
  SecondAngle = 0
FEATURE [Part::MultiFuse] Fusion104  label="m4Cuts003"
  Placement = pos=(0,-3,-37) rot=(0,0,1;0rad)
  Shapes = -> [Cylinder198,Cylinder199,Cylinder200,Cylinder201]
FEATURE [Part::Cylinder] Cylinder202  label="m4HoleBase010"
  Angle = 360
  AttacherType = Attacher::AttachEngine3D
  FirstAngle = 0
  Height = 12
  Placement = pos=(73,26,-7) rot=(0,0.707107,-0.707107;3.14159rad)
  Radius = 5.5
  SecondAngle = 0
FEATURE [Part::Cylinder] Cylinder203  label="m4HoleBase011"
  Angle = 360
  AttacherType = Attacher::AttachEngine3D
  FirstAngle = 0
  Height = 12
  Placement = pos=(5,26,-7) rot=(0,0.707107,-0.707107;3.14159rad)
  Radius = 5.5
  SecondAngle = 0
FEATURE [Part::Cylinder] Cylinder204  label="m4HoleBase012"
  Angle = 360
  AttacherType = Attacher::AttachEngine3D
  FirstAngle = 0
  Height = 12
  Placement = pos=(73,26,104) rot=(0,0.707107,-0.707107;3.14159rad)
  Radius = 5.5
  SecondAngle = 0
FEATURE [Part::Cylinder] Cylinder205  label="m4HoleBase013"
  Angle = 360
  AttacherType = Attacher::AttachEngine3D
  FirstAngle = 0
  Height = 12
  Placement = pos=(5,26,104) rot=(0,0.707107,-0.707107;3.14159rad)
  Radius = 5.5
  SecondAngle = 0
FEATURE [Part::Cylinder] Cylinder206  label="bottomIn002"
  Angle = 90
  AttacherType = Attacher::AttachEngine3D
  FirstAngle = 0
  Height = 60
  Placement = pos=(9,26,111) rot=(0.57735,-0.57735,0.57735;4.18879rad)
  Radius = 5
  SecondAngle = 0
FEATURE [Part::MultiFuse] Fusion105  label="bottomIn"
  Placement = pos=(0,2,0) rot=(0,0,1;0rad)
  Shapes = -> [Cylinder205,Cylinder202,Cylinder203,Cylinder204]
FEATURE [Part::FeaturePython] Tube001  label="bottomCuts004"  # WARN: FeaturePython — macro-defined, semantics opaque (R4)
  AttacherType = Attacher::AttachEngine3D
  Height = 10
  InnerRadius = 5
  OuterRadius = 7
  Placement = pos=(34,26,111) rot=(0,1,0;1.5708rad)
FEATURE [Part::Box] Box108  label="Cube090"
  AttacherType = Attacher::AttachEngine3D
  Height = 12
  Length = 6
  Placement = pos=(3,0,44) rot=(0,0,1;0rad)
  Width = 2
FEATURE [Part::Box] Box109  label="usbCut006"
  AttacherType = Attacher::AttachEngine3D
  Height = 10
  Length = 82
  Width = 20
FEATURE [Part::Box] Box110  label="Cube091"
  AttacherType = Attacher::AttachEngine3D
  Height = 10
  Length = 82
  Width = 5
FEATURE [Part::Box] Box111  label="Cube092"
  AttacherType = Attacher::AttachEngine3D
  Height = 10
  Length = 82
  Width = 5
FEATURE [Part::Box] Box112  label="usbCut007"
  AttacherType = Attacher::AttachEngine3D
  Height = 10
  Length = 82
  Width = 20
FEATURE [Part::Box] Box113  label="Cube093"
  AttacherType = Attacher::AttachEngine3D
  Height = 10
  Length = 82
  Width = 5
FEATURE [Part::Box] Box114  label="Cube094"
  AttacherType = Attacher::AttachEngine3D
  Height = 10
  Length = 82
  Width = 5
FEATURE [Part::Cylinder] Cylinder207
  Angle = 360
  AttacherType = Attacher::AttachEngine3D
  FirstAngle = 0
  Height = 2
  Placement = pos=(6,0,44) rot=(0,0.707107,0.707107;3.14159rad)
  Radius = 3
  SecondAngle = 0
FEATURE [Part::Cylinder] Cylinder208
  Angle = 360
  AttacherType = Attacher::AttachEngine3D
  FirstAngle = 0
  Height = 2
  Placement = pos=(6,1.2e-14,56) rot=(0,0.707107,0.707107;3.14159rad)
  Radius = 3
  SecondAngle = 0
FEATURE [Part::Cylinder] Cylinder209
  Angle = 180
  AttacherType = Attacher::AttachEngine3D
  FirstAngle = 0
  Height = 82
  Placement = pos=(0,5,5) rot=(0.707107,0,0.707107;3.14159rad)
  Radius = 5
  SecondAngle = 0
FEATURE [Part::Cut] Cut141  label="cornerCuts006"
  Base = -> Box110
  Tool = -> Cylinder209
FEATURE [Part::Cylinder] Cylinder210
  Angle = 180
  AttacherType = Attacher::AttachEngine3D
  FirstAngle = 0
  Height = 82
  Placement = pos=(0,5,5) rot=(0.707107,0,0.707107;3.14159rad)
  Radius = 5
  SecondAngle = 0
FEATURE [Part::Cut] Cut142  label="cornerCuts007"
  Base = -> Box111
  Placement = pos=(0,20,10) rot=(1,0,0;3.14159rad)
  Tool = -> Cylinder210
FEATURE [Part::Cylinder] Cylinder211
  Angle = 180
  AttacherType = Attacher::AttachEngine3D
  FirstAngle = 0
  Height = 82
  Placement = pos=(0,5,5) rot=(0.707107,0,0.707107;3.14159rad)
  Radius = 5
  SecondAngle = 0
FEATURE [Part::Cut] Cut144  label="cornerCuts008"
  Base = -> Box113
  Tool = -> Cylinder211
FEATURE [Part::Cylinder] Cylinder212
  Angle = 180
  AttacherType = Attacher::AttachEngine3D
  FirstAngle = 0
  Height = 82
  Placement = pos=(0,5,5) rot=(0.707107,0,0.707107;3.14159rad)
  Radius = 5
  SecondAngle = 0
FEATURE [Part::Cut] Cut145  label="cornerCuts009"
  Base = -> Box114
  Placement = pos=(0,20,10) rot=(1,0,0;3.14159rad)
  Tool = -> Cylinder212
FEATURE [Part::MultiFuse] Fusion106  label="voltaicCut001"
  Placement = pos=(33,24,30.5) rot=(0,0,1;0rad)
  Shapes = -> [Cylinder208,Cylinder207,Box108]
FEATURE [Part::MultiFuse] Fusion107
  Shapes = -> [Cut141,Cut142]
FEATURE [Part::Cut] Cut143  label="usbCut008"
  Base = -> Box109
  Placement = pos=(-50,16,68) rot=(1,0,0;1.5708rad)
  Tool = -> Fusion107
FEATURE [Part::MultiFuse] Fusion108
  Shapes = -> [Cut144,Cut145]
FEATURE [Part::Cut] Cut146  label="usbCut009"
  Base = -> Box112
  Placement = pos=(50,17,68) rot=(1,0,0;1.5708rad)
  Tool = -> Fusion108
FEATURE [Part::MultiFuse] Fusion109  label="bottomCuts005"
  Placement = pos=(0,2,-23) rot=(0,0,1;0rad)
  Shapes = -> [Cut143,Cut146,Fusion106]
FEATURE [Part::MultiFuse] Fusion110  label="bottomCuts006"
  Shapes = -> [Fusion103,Fusion104]
FEATURE [Part::Box] Box115  label="Cube095"
  AttacherType = Attacher::AttachEngine3D
  Height = 2
  Length = 10
  Placement = pos=(0,0,0) rot=(0,-1,0;0.785398rad)
  Width = 10
FEATURE [Part::Box] Box116  label="Cube096"
  AttacherType = Attacher::AttachEngine3D
  Height = 2
  Length = 24
  Placement = pos=(0,0,10) rot=(0,-1,0;0.785398rad)
  Width = 10
FEATURE [Part::Box] Box117  label="Cube097"
  AttacherType = Attacher::AttachEngine3D
  Height = 2
  Length = 12
  Placement = pos=(0,0,20) rot=(0,-1,0;0.785398rad)
  Width = 10
FEATURE [Part::Box] Box118  label="Cube098"
  AttacherType = Attacher::AttachEngine3D
  Height = 2
  Length = 10
  Placement = pos=(0,0,30) rot=(0,-1,0;0.785398rad)
  Width = 10
FEATURE [Part::Box] Box119  label="Cube099"
  AttacherType = Attacher::AttachEngine3D
  Height = 2
  Length = 10
  Placement = pos=(0,0,40) rot=(0,-1,0;0.785398rad)
  Width = 10
FEATURE [Part::Box] Box120  label="Cube100"
  AttacherType = Attacher::AttachEngine3D
  Height = 2
  Length = 10
  Placement = pos=(0,0,50) rot=(0,-1,0;0.785398rad)
  Width = 10
FEATURE [Part::Box] Box121  label="Cube101"
  AttacherType = Attacher::AttachEngine3D
  Height = 2
  Length = 10
  Placement = pos=(0,0,60) rot=(0,-1,0;0.785398rad)
  Width = 10
FEATURE [Part::Box] Box122  label="Cube102"
  AttacherType = Attacher::AttachEngine3D
  Height = 2
  Length = 10
  Placement = pos=(0,0,70) rot=(0,-1,0;0.785398rad)
  Width = 10
FEATURE [Part::Box] Box123  label="Cube103"
  AttacherType = Attacher::AttachEngine3D
  Height = 2
  Length = 10
  Placement = pos=(0,0,80) rot=(0,-1,0;0.785398rad)
  Width = 10
FEATURE [Part::Box] Box124  label="Cube104"
  AttacherType = Attacher::AttachEngine3D
  Height = 2
  Length = 10
  Placement = pos=(0,0,90) rot=(0,-1,0;0.785398rad)
  Width = 10
FEATURE [Part::Box] Box125  label="Cube105"
  AttacherType = Attacher::AttachEngine3D
  Height = 2
  Length = 10
  Placement = pos=(0,0,1000) rot=(0,-1,0;0.785398rad)
  Width = 10
FEATURE [Part::Box] Box126  label="Cube106"
  AttacherType = Attacher::AttachEngine3D
  Height = 2
  Length = 10
  Placement = pos=(0,0,0) rot=(0,-1,0;0.785398rad)
  Width = 10
FEATURE [Part::Box] Box127  label="Cube107"
  AttacherType = Attacher::AttachEngine3D
  Height = 2
  Length = 26
  Placement = pos=(0,0,10) rot=(0,-1,0;0.785398rad)
  Width = 10
FEATURE [Part::Box] Box128  label="Cube108"
  AttacherType = Attacher::AttachEngine3D
  Height = 2
  Length = 12
  Placement = pos=(0,0,20) rot=(0,-1,0;0.785398rad)
  Width = 10
FEATURE [Part::Box] Box129  label="Cube109"
  AttacherType = Attacher::AttachEngine3D
  Height = 2
  Length = 10
  Placement = pos=(0,0,30) rot=(0,-1,0;0.785398rad)
  Width = 10
FEATURE [Part::Box] Box130  label="Cube110"
  AttacherType = Attacher::AttachEngine3D
  Height = 2
  Length = 10
  Placement = pos=(0,0,40) rot=(0,-1,0;0.785398rad)
  Width = 10
FEATURE [Part::Box] Box131  label="Cube111"
  AttacherType = Attacher::AttachEngine3D
  Height = 2
  Length = 10
  Placement = pos=(0,0,50) rot=(0,-1,0;0.785398rad)
  Width = 10
FEATURE [Part::Box] Box132  label="Cube112"
  AttacherType = Attacher::AttachEngine3D
  Height = 2
  Length = 10
  Placement = pos=(0,0,60) rot=(0,-1,0;0.785398rad)
  Width = 10
FEATURE [Part::Box] Box133  label="Cube113"
  AttacherType = Attacher::AttachEngine3D
  Height = 2
  Length = 10
  Placement = pos=(0,0,70) rot=(0,-1,0;0.785398rad)
  Width = 10
FEATURE [Part::Box] Box134  label="Cube114"
  AttacherType = Attacher::AttachEngine3D
  Height = 2
  Length = 10
  Placement = pos=(0,0,80) rot=(0,-1,0;0.785398rad)
  Width = 10
FEATURE [Part::Box] Box135  label="Cube115"
  AttacherType = Attacher::AttachEngine3D
  Height = 2
  Length = 10
  Placement = pos=(0,0,90) rot=(0,-1,0;0.785398rad)
  Width = 10
FEATURE [Part::Box] Box136  label="Cube116"
  AttacherType = Attacher::AttachEngine3D
  Height = 2
  Length = 10
  Placement = pos=(0,0,1000) rot=(0,-1,0;0.785398rad)
  Width = 10
FEATURE [Part::MultiFuse] Fusion111  label="vents002"
  Placement = pos=(-4,-10,15) rot=(0,0,1;0rad)
  Shapes = -> [Box115,Box116,Box117,Box118,Box119,Box120,Box121,Box122,Box123,Box124,Box125]
FEATURE [Part::MultiFuse] Fusion112  label="vents003"
  Placement = pos=(82,0,15) rot=(0,0,1;3.14159rad)
  Shapes = -> [Box126,Box127,Box128,Box129,Box130,Box131,Box132,Box133,Box134,Box135,Box136]
FEATURE [Part::MultiFuse] Fusion113  label="topCuts001"
  Placement = pos=(0,-7,-53) rot=(0,0,1;0rad)
  Shapes = -> [Fusion111,Fusion112]
FEATURE [Part::Cylinder] Cylinder213  label="topCuts002"
  Angle = 360
  AttacherType = Attacher::AttachEngine3D
  FirstAngle = 0
  Height = 10
  Placement = pos=(88,-8,84) rot=(0,-1,0;1.5708rad)
  Radius = 10
  SecondAngle = 0
FEATURE [Part::Box] Box137  label="Cube117"
  AttacherType = Attacher::AttachEngine3D
  Height = 1.5
  Length = 36
  Width = 29
FEATURE [Part::Box] Box138  label="Cube118"
  AttacherType = Attacher::AttachEngine3D
  Height = 5.5
  Length = 36
  Placement = pos=(0,0,3.6) rot=(0,0,1;0rad)
  Width = 29
FEATURE [Part::Feature] logo3mmWidth001_solid001  label="logo3mmWidth001 (Solid)001"
  shape: bbox 30 x 22.21 x 4.944 mm, 7244 faces (baked)
FEATURE [Part::MultiFuse] Fusion114
  Shapes = -> [Box137,logo3mmWidth001_solid001]
FEATURE [Part::Cut] Cut147  label="topCuts003"
  Base = -> Fusion114
  Placement = pos=(21,-16.5,7) rot=(1,0,0;1.5708rad)
  Tool = -> Box138
FEATURE [Part::MultiFuse] Fusion115  label="topCuts004"
  Shapes = -> [Cut147,Fusion113,Cylinder213]
FEATURE [Part::MultiFuse] Fusion116  label="topIn003"
  Shapes = -> [Fusion101,Fusion092,Cut100,Cut099]
FEATURE [Part::Cut] Cut148  label="top005"
  Base = -> Fusion116
  Tool = -> Fusion115
FEATURE [Part::MultiFuse] Fusion117  label="bottomCuts007"
  Shapes = -> [Fusion110,Tube001,Fusion109]
FEATURE [Part::MultiFuse] Fusion118  label="bottom004"
  Shapes = -> [Fusion105,Fusion102,Cylinder206,Cut135]
FEATURE [Part::Cut] Cut149  label="bottom005"
  Base = -> Fusion118
  Tool = -> Fusion117
FEATURE [Part::MultiFuse] Fusion119
  Shapes = -> [Cut148,Cut149]
FEATURE [Mesh::Feature] _9PerLeaf_Design  label="99PerLeaf Design"
  Placement = pos=(34.25,-16.4,20.25) rot=(1,0,0;1.5708rad)
FEATURE [Mesh::Feature] _00G1Design  label="100G1Design"
  Placement = pos=(34,-16.58,20.2) rot=(1,0,0;1.5708rad)
FEATURE [Mesh::Feature] test2
  Placement = pos=(-20,-20,44) rot=(-1,0,0;1.5708rad)
